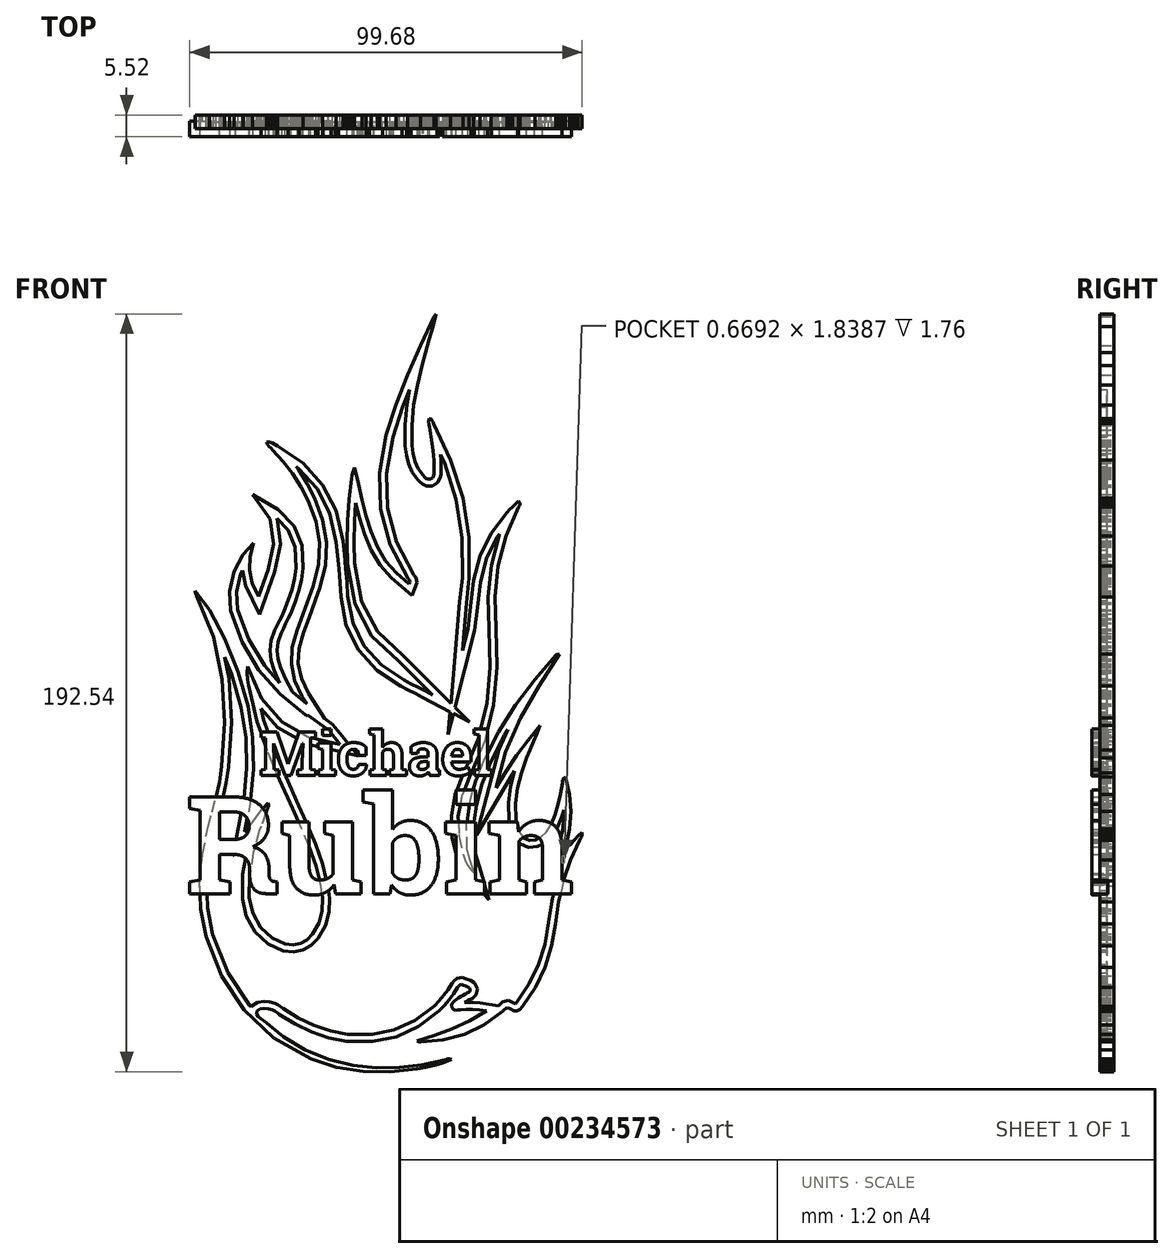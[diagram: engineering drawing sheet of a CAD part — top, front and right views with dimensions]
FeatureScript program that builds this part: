
annotation { "Feature Type Name" : "Feature", "Feature Type Description" : "" }
export const myFeature = defineFeature(function(context is Context, id is Id, definition is map)
    precondition{}
    {
        {
            var Q0;
            Q0=qCreatedBy(makeId("Front.planeOp"),FACE);
            var sketch = newSketch(context, id + "F0", { "sketchPlane" : qUnion([Q0])});
            skLineSegment(sketch, "E0", {"start": v(36.22, -211.62) * mm, "end": v(31.33, -213.63) * mm});
            skLineSegment(sketch, "E1", {"start": v(31.33, -213.63) * mm, "end": v(26.4, -215.17) * mm});
            skLineSegment(sketch, "E2", {"start": v(26.4, -215.17) * mm, "end": v(21.44, -216.32) * mm});
            skLineSegment(sketch, "E3", {"start": v(21.44, -216.32) * mm, "end": v(16.46, -217.18) * mm});
            skLineSegment(sketch, "E4", {"start": v(16.46, -217.18) * mm, "end": v(0.82, -218.8) * mm});
            skLineSegment(sketch, "E5", {"start": v(0.82, -218.8) * mm, "end": v(-14.67, -218.69) * mm});
            skLineSegment(sketch, "E6", {"start": v(-14.67, -218.69) * mm, "end": v(-29.95, -216.4) * mm});
            skLineSegment(sketch, "E7", {"start": v(-29.95, -216.4) * mm, "end": v(-44.93, -211.45) * mm});
            skLineSegment(sketch, "E8", {"start": v(-44.93, -211.45) * mm, "end": v(-66.37, -199.2) * mm});
            skLineSegment(sketch, "E9", {"start": v(-66.37, -199.2) * mm, "end": v(-83.45, -183.16) * mm});
            skLineSegment(sketch, "E10", {"start": v(-83.45, -183.16) * mm, "end": v(-96.43, -163.58) * mm});
            skLineSegment(sketch, "E11", {"start": v(-96.43, -163.58) * mm, "end": v(-105.51, -140.68) * mm});
            skLineSegment(sketch, "E12", {"start": v(-105.51, -140.68) * mm, "end": v(-108.67, -124.82) * mm});
            skLineSegment(sketch, "E13", {"start": v(-108.67, -124.82) * mm, "end": v(-109.13, -109.02) * mm});
            skLineSegment(sketch, "E14", {"start": v(-109.13, -109.02) * mm, "end": v(-107.45, -93.26) * mm});
            skLineSegment(sketch, "E15", {"start": v(-107.45, -93.26) * mm, "end": v(-104.2, -77.54) * mm});
            skLineSegment(sketch, "E16", {"start": v(-104.2, -77.54) * mm, "end": v(-101.94, -68.84) * mm});
            skLineSegment(sketch, "E17", {"start": v(-101.94, -68.84) * mm, "end": v(-99.7, -60.13) * mm});
            skLineSegment(sketch, "E18", {"start": v(-99.7, -60.13) * mm, "end": v(-97.73, -51.36) * mm});
            skLineSegment(sketch, "E19", {"start": v(-97.73, -51.36) * mm, "end": v(-96.35, -42.46) * mm});
            skLineSegment(sketch, "E20", {"start": v(-96.35, -42.46) * mm, "end": v(-94.74, -17.12) * mm});
            skLineSegment(sketch, "E21", {"start": v(-94.74, -17.12) * mm, "end": v(-96.1, 7.8) * mm});
            skLineSegment(sketch, "E22", {"start": v(-96.1, 7.8) * mm, "end": v(-101.2, 32.15) * mm});
            skLineSegment(sketch, "E23", {"start": v(-101.2, 32.15) * mm, "end": v(-110.82, 55.85) * mm});
            skLineSegment(sketch, "E24", {"start": v(-110.82, 55.85) * mm, "end": v(-111.04, 56.3) * mm});
            skLineSegment(sketch, "E25", {"start": v(-111.04, 56.3) * mm, "end": v(-111.25, 56.75) * mm});
            skLineSegment(sketch, "E26", {"start": v(-111.25, 56.75) * mm, "end": v(-111.45, 57.2) * mm});
            skLineSegment(sketch, "E27", {"start": v(-111.45, 57.2) * mm, "end": v(-111.63, 57.67) * mm});
            skLineSegment(sketch, "E28", {"start": v(-111.63, 57.67) * mm, "end": v(-111.68, 57.9) * mm});
            skLineSegment(sketch, "E29", {"start": v(-111.68, 57.9) * mm, "end": v(-111.7, 58.14) * mm});
            skLineSegment(sketch, "E30", {"start": v(-111.7, 58.14) * mm, "end": v(-111.7, 58.38) * mm});
            skLineSegment(sketch, "E31", {"start": v(-111.7, 58.38) * mm, "end": v(-111.71, 58.63) * mm});
            skLineSegment(sketch, "E32", {"start": v(-111.71, 58.63) * mm, "end": v(-103.48, 47.66) * mm});
            skLineSegment(sketch, "E33", {"start": v(-103.48, 47.66) * mm, "end": v(-94.75, 31.33) * mm});
            skLineSegment(sketch, "E34", {"start": v(-94.75, 31.33) * mm, "end": v(-86.88, 12.12) * mm});
            skLineSegment(sketch, "E35", {"start": v(-86.88, 12.12) * mm, "end": v(-81.23, -7.5) * mm});
            skLineSegment(sketch, "E36", {"start": v(-81.23, -7.5) * mm, "end": v(-78.47, -25.75) * mm});
            skLineSegment(sketch, "E37", {"start": v(-78.47, -25.75) * mm, "end": v(-77.98, -43.94) * mm});
            skLineSegment(sketch, "E38", {"start": v(-77.98, -43.94) * mm, "end": v(-79.6, -62.1) * mm});
            skLineSegment(sketch, "E39", {"start": v(-79.6, -62.1) * mm, "end": v(-83.23, -80.25) * mm});
            skLineSegment(sketch, "E40", {"start": v(-83.23, -80.25) * mm, "end": v(-79.71, -76.18) * mm});
            skLineSegment(sketch, "E41", {"start": v(-79.71, -76.18) * mm, "end": v(-76.5, -71.93) * mm});
            skLineSegment(sketch, "E42", {"start": v(-76.5, -71.93) * mm, "end": v(-73.28, -67.72) * mm});
            skLineSegment(sketch, "E43", {"start": v(-73.28, -67.72) * mm, "end": v(-69.75, -63.75) * mm});
            skLineSegment(sketch, "E44", {"start": v(-69.75, -63.75) * mm, "end": v(-69.26, -64.86) * mm});
            skLineSegment(sketch, "E45", {"start": v(-69.26, -64.86) * mm, "end": v(-69.38, -65.8) * mm});
            skLineSegment(sketch, "E46", {"start": v(-69.38, -65.8) * mm, "end": v(-69.82, -66.66) * mm});
            skLineSegment(sketch, "E47", {"start": v(-69.82, -66.66) * mm, "end": v(-70.24, -67.47) * mm});
            skLineSegment(sketch, "E48", {"start": v(-70.24, -67.47) * mm, "end": v(-74.68, -79.84) * mm});
            skLineSegment(sketch, "E49", {"start": v(-74.68, -79.84) * mm, "end": v(-78.17, -92.4) * mm});
            skLineSegment(sketch, "E50", {"start": v(-78.17, -92.4) * mm, "end": v(-80.25, -105.26) * mm});
            skLineSegment(sketch, "E51", {"start": v(-80.25, -105.26) * mm, "end": v(-80.49, -118.5) * mm});
            skLineSegment(sketch, "E52", {"start": v(-80.49, -118.5) * mm, "end": v(-78.44, -127.45) * mm});
            skLineSegment(sketch, "E53", {"start": v(-78.44, -127.45) * mm, "end": v(-73.87, -135.48) * mm});
            skLineSegment(sketch, "E54", {"start": v(-73.87, -135.48) * mm, "end": v(-67.44, -141.67) * mm});
            skLineSegment(sketch, "E55", {"start": v(-67.44, -141.67) * mm, "end": v(-59.81, -145.14) * mm});
            skLineSegment(sketch, "E56", {"start": v(-59.81, -145.14) * mm, "end": v(-55.14, -145.6) * mm});
            skLineSegment(sketch, "E57", {"start": v(-55.14, -145.6) * mm, "end": v(-50.93, -144.78) * mm});
            skLineSegment(sketch, "E58", {"start": v(-50.93, -144.78) * mm, "end": v(-47.2, -142.69) * mm});
            skLineSegment(sketch, "E59", {"start": v(-47.2, -142.69) * mm, "end": v(-43.94, -139.34) * mm});
            skLineSegment(sketch, "E60", {"start": v(-43.94, -139.34) * mm, "end": v(-40.24, -132.83) * mm});
            skLineSegment(sketch, "E61", {"start": v(-40.24, -132.83) * mm, "end": v(-38.48, -125.96) * mm});
            skLineSegment(sketch, "E62", {"start": v(-38.48, -125.96) * mm, "end": v(-38.25, -118.85) * mm});
            skLineSegment(sketch, "E63", {"start": v(-38.25, -118.85) * mm, "end": v(-39.12, -111.62) * mm});
            skLineSegment(sketch, "E64", {"start": v(-39.12, -111.62) * mm, "end": v(-41.97, -99.94) * mm});
            skLineSegment(sketch, "E65", {"start": v(-41.97, -99.94) * mm, "end": v(-45.97, -88.66) * mm});
            skLineSegment(sketch, "E66", {"start": v(-45.97, -88.66) * mm, "end": v(-50.67, -77.63) * mm});
            skLineSegment(sketch, "E67", {"start": v(-50.67, -77.63) * mm, "end": v(-55.6, -66.69) * mm});
            skLineSegment(sketch, "E68", {"start": v(-55.6, -66.69) * mm, "end": v(-62.97, -50.27) * mm});
            skLineSegment(sketch, "E69", {"start": v(-62.97, -50.27) * mm, "end": v(-69.97, -33.73) * mm});
            skLineSegment(sketch, "E70", {"start": v(-69.97, -33.73) * mm, "end": v(-75.91, -16.8) * mm});
            skLineSegment(sketch, "E71", {"start": v(-75.91, -16.8) * mm, "end": v(-80.13, 0.76) * mm});
            skLineSegment(sketch, "E72", {"start": v(-80.13, 0.76) * mm, "end": v(-80.78, 4.25) * mm});
            skLineSegment(sketch, "E73", {"start": v(-80.78, 4.25) * mm, "end": v(-81.36, 7.8) * mm});
            skLineSegment(sketch, "E74", {"start": v(-81.36, 7.8) * mm, "end": v(-81.65, 11.46) * mm});
            skLineSegment(sketch, "E75", {"start": v(-81.65, 11.46) * mm, "end": v(-81.44, 15.32) * mm});
            skLineSegment(sketch, "E76", {"start": v(-81.44, 15.32) * mm, "end": v(-73.38, -3.27) * mm});
            skLineSegment(sketch, "E77", {"start": v(-73.38, -3.27) * mm, "end": v(-61.5, -16.8) * mm});
            skLineSegment(sketch, "E78", {"start": v(-61.5, -16.8) * mm, "end": v(-46.23, -25.6) * mm});
            skLineSegment(sketch, "E79", {"start": v(-46.23, -25.6) * mm, "end": v(-28, -29.97) * mm});
            skLineSegment(sketch, "E80", {"start": v(-28, -29.97) * mm, "end": v(-30.14, -27.34) * mm});
            skLineSegment(sketch, "E81", {"start": v(-30.14, -27.34) * mm, "end": v(-32.52, -24.4) * mm});
            skLineSegment(sketch, "E82", {"start": v(-32.52, -24.4) * mm, "end": v(-35.1, -21.27) * mm});
            skLineSegment(sketch, "E83", {"start": v(-47.22, -6.45) * mm, "end": v(-49.9, -2.22) * mm});
            skLineSegment(sketch, "E84", {"start": v(-49.9, -2.22) * mm, "end": v(-54.2, 7.07) * mm});
            skLineSegment(sketch, "E85", {"start": v(-54.2, 7.07) * mm, "end": v(-56.2, 16.53) * mm});
            skLineSegment(sketch, "E86", {"start": v(-56.2, 16.53) * mm, "end": v(-55.8, 26.19) * mm});
            skLineSegment(sketch, "E87", {"start": v(-55.8, 26.19) * mm, "end": v(-52.98, 36.09) * mm});
            skLineSegment(sketch, "E88", {"start": v(-52.98, 36.09) * mm, "end": v(-50.54, 42.37) * mm});
            skLineSegment(sketch, "E89", {"start": v(-50.54, 42.37) * mm, "end": v(-48.24, 48.72) * mm});
            skLineSegment(sketch, "E90", {"start": v(-48.24, 48.72) * mm, "end": v(-45.98, 55.08) * mm});
            skLineSegment(sketch, "E91", {"start": v(-45.98, 55.08) * mm, "end": v(-43.67, 61.42) * mm});
            skLineSegment(sketch, "E92", {"start": v(-43.67, 61.42) * mm, "end": v(-40.4, 74.02) * mm});
            skLineSegment(sketch, "E93", {"start": v(-40.4, 74.02) * mm, "end": v(-39.92, 86.47) * mm});
            skLineSegment(sketch, "E94", {"start": v(-39.92, 86.47) * mm, "end": v(-42, 98.76) * mm});
            skLineSegment(sketch, "E95", {"start": v(-42, 98.76) * mm, "end": v(-46.45, 110.92) * mm});
            skLineSegment(sketch, "E96", {"start": v(-46.45, 110.92) * mm, "end": v(-50.6, 118.94) * mm});
            skLineSegment(sketch, "E97", {"start": v(-50.6, 118.94) * mm, "end": v(-55.4, 126.5) * mm});
            skLineSegment(sketch, "E98", {"start": v(-55.4, 126.5) * mm, "end": v(-60.87, 133.6) * mm});
            skLineSegment(sketch, "E99", {"start": v(-60.87, 133.6) * mm, "end": v(-66.94, 140.29) * mm});
            skLineSegment(sketch, "E100", {"start": v(-66.94, 140.29) * mm, "end": v(-67.94, 141.2) * mm});
            skLineSegment(sketch, "E101", {"start": v(-67.94, 141.2) * mm, "end": v(-68.96, 142.15) * mm});
            skLineSegment(sketch, "E102", {"start": v(-68.96, 142.15) * mm, "end": v(-69.86, 143.3) * mm});
            skLineSegment(sketch, "E103", {"start": v(-69.86, 143.3) * mm, "end": v(-70.49, 144.84) * mm});
            skLineSegment(sketch, "E104", {"start": v(-70.49, 144.84) * mm, "end": v(-68.66, 144.75) * mm});
            skLineSegment(sketch, "E105", {"start": v(-68.66, 144.75) * mm, "end": v(-67.03, 144.2) * mm});
            skLineSegment(sketch, "E106", {"start": v(-67.03, 144.2) * mm, "end": v(-65.55, 143.41) * mm});
            skLineSegment(sketch, "E107", {"start": v(-65.55, 143.41) * mm, "end": v(-64.11, 142.6) * mm});
            skLineSegment(sketch, "E108", {"start": v(-64.11, 142.6) * mm, "end": v(-49.3, 132.58) * mm});
            skLineSegment(sketch, "E109", {"start": v(-49.3, 132.58) * mm, "end": v(-38.08, 120.08) * mm});
            skLineSegment(sketch, "E110", {"start": v(-38.08, 120.08) * mm, "end": v(-30.44, 105.13) * mm});
            skLineSegment(sketch, "E111", {"start": v(-30.44, 105.13) * mm, "end": v(-26.4, 87.74) * mm});
            skLineSegment(sketch, "E112", {"start": v(-26.4, 87.74) * mm, "end": v(-25.52, 79.8) * mm});
            skLineSegment(sketch, "E113", {"start": v(-25.52, 79.8) * mm, "end": v(-24.78, 71.84) * mm});
            skLineSegment(sketch, "E114", {"start": v(-24.78, 71.84) * mm, "end": v(-24.15, 63.88) * mm});
            skLineSegment(sketch, "E115", {"start": v(-24.15, 63.88) * mm, "end": v(-23.61, 55.9) * mm});
            skLineSegment(sketch, "E116", {"start": v(-23.61, 55.9) * mm, "end": v(-20.68, 40.23) * mm});
            skLineSegment(sketch, "E117", {"start": v(-20.68, 40.23) * mm, "end": v(-14.12, 27) * mm});
            skLineSegment(sketch, "E118", {"start": v(-14.12, 27) * mm, "end": v(-4.17, 16.07) * mm});
            skLineSegment(sketch, "E119", {"start": v(-4.17, 16.07) * mm, "end": v(8.95, 7.26) * mm});
            skLineSegment(sketch, "E120", {"start": v(8.95, 7.26) * mm, "end": v(13.05, 5.13) * mm});
            skLineSegment(sketch, "E121", {"start": v(13.05, 5.13) * mm, "end": v(17.18, 3.04) * mm});
            skLineSegment(sketch, "E122", {"start": v(17.18, 3.04) * mm, "end": v(21.3, 0.95) * mm});
            skLineSegment(sketch, "E123", {"start": v(21.3, 0.95) * mm, "end": v(25.39, -1.2) * mm});
            skLineSegment(sketch, "E124", {"start": v(42.57, 24.32) * mm, "end": v(45.76, 36.8) * mm});
            skLineSegment(sketch, "E125", {"start": v(45.76, 36.8) * mm, "end": v(47.38, 49.8) * mm});
            skLineSegment(sketch, "E126", {"start": v(47.38, 49.8) * mm, "end": v(49.12, 64.7) * mm});
            skLineSegment(sketch, "E127", {"start": v(49.12, 64.7) * mm, "end": v(52.83, 78.86) * mm});
            skLineSegment(sketch, "E128", {"start": v(52.83, 78.86) * mm, "end": v(59.04, 92.06) * mm});
            skLineSegment(sketch, "E129", {"start": v(59.04, 92.06) * mm, "end": v(68.25, 104.1) * mm});
            skLineSegment(sketch, "E130", {"start": v(68.25, 104.1) * mm, "end": v(69.9, 105.76) * mm});
            skLineSegment(sketch, "E131", {"start": v(69.9, 105.76) * mm, "end": v(71.6, 107.38) * mm});
            skLineSegment(sketch, "E132", {"start": v(71.6, 107.38) * mm, "end": v(73.33, 108.98) * mm});
            skLineSegment(sketch, "E133", {"start": v(73.33, 108.98) * mm, "end": v(75.04, 110.6) * mm});
            skLineSegment(sketch, "E134", {"start": v(75.04, 110.6) * mm, "end": v(75.8, 109.58) * mm});
            skLineSegment(sketch, "E135", {"start": v(75.8, 109.58) * mm, "end": v(75.83, 108.72) * mm});
            skLineSegment(sketch, "E136", {"start": v(75.83, 108.72) * mm, "end": v(75.46, 107.99) * mm});
            skLineSegment(sketch, "E137", {"start": v(75.46, 107.99) * mm, "end": v(75.03, 107.33) * mm});
            skLineSegment(sketch, "E138", {"start": v(75.03, 107.33) * mm, "end": v(67.67, 90.5) * mm});
            skLineSegment(sketch, "E139", {"start": v(67.67, 90.5) * mm, "end": v(63.25, 73.12) * mm});
            skLineSegment(sketch, "E140", {"start": v(63.25, 73.12) * mm, "end": v(61.45, 55.28) * mm});
            skLineSegment(sketch, "E141", {"start": v(61.45, 55.28) * mm, "end": v(61.96, 37.07) * mm});
            skLineSegment(sketch, "E142", {"start": v(61.96, 37.07) * mm, "end": v(62.65, 14.79) * mm});
            skLineSegment(sketch, "E143", {"start": v(62.65, 14.79) * mm, "end": v(60.62, -6.94) * mm});
            skLineSegment(sketch, "E144", {"start": v(60.62, -6.94) * mm, "end": v(55.44, -28.12) * mm});
            skLineSegment(sketch, "E145", {"start": v(55.44, -28.12) * mm, "end": v(46.7, -48.74) * mm});
            skLineSegment(sketch, "E146", {"start": v(46.7, -48.74) * mm, "end": v(42.2, -59.87) * mm});
            skLineSegment(sketch, "E147", {"start": v(42.2, -59.87) * mm, "end": v(40.19, -71.32) * mm});
            skLineSegment(sketch, "E148", {"start": v(40.19, -71.32) * mm, "end": v(40.61, -83) * mm});
            skLineSegment(sketch, "E149", {"start": v(40.61, -83) * mm, "end": v(43.43, -94.83) * mm});
            skLineSegment(sketch, "E150", {"start": v(43.43, -94.83) * mm, "end": v(44.5, -97.48) * mm});
            skLineSegment(sketch, "E151", {"start": v(44.5, -97.48) * mm, "end": v(45.83, -99.98) * mm});
            skLineSegment(sketch, "E152", {"start": v(45.83, -99.98) * mm, "end": v(47.47, -102.3) * mm});
            skLineSegment(sketch, "E153", {"start": v(47.47, -102.3) * mm, "end": v(49.44, -104.44) * mm});
            skLineSegment(sketch, "E154", {"start": v(49.44, -104.44) * mm, "end": v(48.39, -100.83) * mm});
            skLineSegment(sketch, "E155", {"start": v(48.39, -100.83) * mm, "end": v(47.2, -97.27) * mm});
            skLineSegment(sketch, "E156", {"start": v(47.2, -97.27) * mm, "end": v(46.1, -93.68) * mm});
            skLineSegment(sketch, "E157", {"start": v(46.1, -93.68) * mm, "end": v(45.39, -89.98) * mm});
            skLineSegment(sketch, "E158", {"start": v(45.39, -89.98) * mm, "end": v(45, -76.7) * mm});
            skLineSegment(sketch, "E159", {"start": v(45, -76.7) * mm, "end": v(46.72, -63.83) * mm});
            skLineSegment(sketch, "E160", {"start": v(46.72, -63.83) * mm, "end": v(50.17, -51.3) * mm});
            skLineSegment(sketch, "E161", {"start": v(50.17, -51.3) * mm, "end": v(54.97, -39.06) * mm});
            skLineSegment(sketch, "E162", {"start": v(54.97, -39.06) * mm, "end": v(63.36, -22.5) * mm});
            skLineSegment(sketch, "E163", {"start": v(63.36, -22.5) * mm, "end": v(73.26, -6.97) * mm});
            skLineSegment(sketch, "E164", {"start": v(73.26, -6.97) * mm, "end": v(84.41, 7.72) * mm});
            skLineSegment(sketch, "E165", {"start": v(84.41, 7.72) * mm, "end": v(96.56, 21.71) * mm});
            skLineSegment(sketch, "E166", {"start": v(96.56, 21.71) * mm, "end": v(96.76, 21.85) * mm});
            skLineSegment(sketch, "E167", {"start": v(96.76, 21.85) * mm, "end": v(97.11, 21.99) * mm});
            skLineSegment(sketch, "E168", {"start": v(97.11, 21.99) * mm, "end": v(97.69, 22.19) * mm});
            skLineSegment(sketch, "E169", {"start": v(97.69, 22.19) * mm, "end": v(98.57, 22.52) * mm});
            skLineSegment(sketch, "E170", {"start": v(98.57, 22.52) * mm, "end": v(86.8, 4.05) * mm});
            skLineSegment(sketch, "E171", {"start": v(86.8, 4.05) * mm, "end": v(76.17, -14.66) * mm});
            skLineSegment(sketch, "E172", {"start": v(76.17, -14.66) * mm, "end": v(67.6, -34.16) * mm});
            skLineSegment(sketch, "E173", {"start": v(67.6, -34.16) * mm, "end": v(62.07, -54.97) * mm});
            skLineSegment(sketch, "E174", {"start": v(62.07, -54.97) * mm, "end": v(67.68, -45.45) * mm});
            skLineSegment(sketch, "E175", {"start": v(67.68, -45.45) * mm, "end": v(73.74, -36.24) * mm});
            skLineSegment(sketch, "E176", {"start": v(73.74, -36.24) * mm, "end": v(80.33, -27.4) * mm});
            skLineSegment(sketch, "E177", {"start": v(80.33, -27.4) * mm, "end": v(87.52, -18.94) * mm});
            skLineSegment(sketch, "E178", {"start": v(87.52, -18.94) * mm, "end": v(85.53, -23.6) * mm});
            skLineSegment(sketch, "E179", {"start": v(85.53, -23.6) * mm, "end": v(83.53, -28.25) * mm});
            skLineSegment(sketch, "E180", {"start": v(83.53, -28.25) * mm, "end": v(81.56, -32.91) * mm});
            skLineSegment(sketch, "E181", {"start": v(81.56, -32.91) * mm, "end": v(79.66, -37.6) * mm});
            skLineSegment(sketch, "E182", {"start": v(79.66, -37.6) * mm, "end": v(76.58, -46.2) * mm});
            skLineSegment(sketch, "E183", {"start": v(76.58, -46.2) * mm, "end": v(74.32, -54.96) * mm});
            skLineSegment(sketch, "E184", {"start": v(74.32, -54.96) * mm, "end": v(73.2, -63.92) * mm});
            skLineSegment(sketch, "E185", {"start": v(73.2, -63.92) * mm, "end": v(73.53, -73.14) * mm});
            skLineSegment(sketch, "E186", {"start": v(73.53, -73.14) * mm, "end": v(74.54, -77.85) * mm});
            skLineSegment(sketch, "E187", {"start": v(74.54, -77.85) * mm, "end": v(76.22, -81.55) * mm});
            skLineSegment(sketch, "E188", {"start": v(76.22, -81.55) * mm, "end": v(78.53, -84.06) * mm});
            skLineSegment(sketch, "E189", {"start": v(78.53, -84.06) * mm, "end": v(81.4, -85.22) * mm});
            skLineSegment(sketch, "E190", {"start": v(81.4, -85.22) * mm, "end": v(84.75, -84.93) * mm});
            skLineSegment(sketch, "E191", {"start": v(84.75, -84.93) * mm, "end": v(88.08, -83.26) * mm});
            skLineSegment(sketch, "E192", {"start": v(88.08, -83.26) * mm, "end": v(91.12, -80.4) * mm});
            skLineSegment(sketch, "E193", {"start": v(91.12, -80.4) * mm, "end": v(93.6, -76.56) * mm});
            skLineSegment(sketch, "E194", {"start": v(93.6, -76.56) * mm, "end": v(96.06, -70.66) * mm});
            skLineSegment(sketch, "E195", {"start": v(96.06, -70.66) * mm, "end": v(97.89, -64.58) * mm});
            skLineSegment(sketch, "E196", {"start": v(97.89, -64.58) * mm, "end": v(99.25, -58.37) * mm});
            skLineSegment(sketch, "E197", {"start": v(99.25, -58.37) * mm, "end": v(100.34, -52.08) * mm});
            skLineSegment(sketch, "E198", {"start": v(100.34, -52.08) * mm, "end": v(100.4, -51.25) * mm});
            skLineSegment(sketch, "E199", {"start": v(100.4, -51.25) * mm, "end": v(100.5, -50.37) * mm});
            skLineSegment(sketch, "E200", {"start": v(100.5, -50.37) * mm, "end": v(100.95, -49.5) * mm});
            skLineSegment(sketch, "E201", {"start": v(100.95, -49.5) * mm, "end": v(102, -48.7) * mm});
            skLineSegment(sketch, "E202", {"start": v(102, -48.7) * mm, "end": v(104.38, -58.6) * mm});
            skLineSegment(sketch, "E203", {"start": v(104.38, -58.6) * mm, "end": v(105.2, -68.56) * mm});
            skLineSegment(sketch, "E204", {"start": v(105.2, -68.56) * mm, "end": v(104.5, -78.65) * mm});
            skLineSegment(sketch, "E205", {"start": v(104.5, -78.65) * mm, "end": v(102.35, -88.96) * mm});
            skLineSegment(sketch, "E206", {"start": v(102.35, -88.96) * mm, "end": v(105.22, -87.14) * mm});
            skLineSegment(sketch, "E207", {"start": v(105.22, -87.14) * mm, "end": v(107.32, -84.86) * mm});
            skLineSegment(sketch, "E208", {"start": v(107.32, -84.86) * mm, "end": v(109.25, -82.56) * mm});
            skLineSegment(sketch, "E209", {"start": v(109.25, -82.56) * mm, "end": v(111.61, -80.72) * mm});
            skLineSegment(sketch, "E210", {"start": v(111.61, -80.72) * mm, "end": v(111.71, -82.05) * mm});
            skLineSegment(sketch, "E211", {"start": v(111.71, -82.05) * mm, "end": v(111.37, -83.19) * mm});
            skLineSegment(sketch, "E212", {"start": v(111.37, -83.19) * mm, "end": v(110.8, -84.2) * mm});
            skLineSegment(sketch, "E213", {"start": v(110.8, -84.2) * mm, "end": v(110.22, -85.16) * mm});
            skLineSegment(sketch, "E214", {"start": v(110.22, -85.16) * mm, "end": v(104.88, -96.66) * mm});
            skLineSegment(sketch, "E215", {"start": v(104.88, -96.66) * mm, "end": v(100.95, -108.55) * mm});
            skLineSegment(sketch, "E216", {"start": v(100.95, -108.55) * mm, "end": v(98.19, -120.79) * mm});
            skLineSegment(sketch, "E217", {"start": v(98.19, -120.79) * mm, "end": v(96.34, -133.33) * mm});
            skLineSegment(sketch, "E218", {"start": v(96.34, -133.33) * mm, "end": v(94.07, -146.18) * mm});
            skLineSegment(sketch, "E219", {"start": v(94.07, -146.18) * mm, "end": v(90.2, -158.45) * mm});
            skLineSegment(sketch, "E220", {"start": v(90.2, -158.45) * mm, "end": v(84.66, -170.07) * mm});
            skLineSegment(sketch, "E221", {"start": v(84.66, -170.07) * mm, "end": v(77.33, -180.99) * mm});
            skLineSegment(sketch, "E222", {"start": v(77.33, -180.99) * mm, "end": v(75.79, -182.68) * mm});
            skLineSegment(sketch, "E223", {"start": v(75.79, -182.68) * mm, "end": v(74.16, -183.69) * mm});
            skLineSegment(sketch, "E224", {"start": v(74.16, -183.69) * mm, "end": v(72.35, -183.76) * mm});
            skLineSegment(sketch, "E225", {"start": v(72.35, -183.76) * mm, "end": v(70.27, -182.65) * mm});
            skLineSegment(sketch, "E226", {"start": v(70.27, -182.65) * mm, "end": v(68.78, -181.95) * mm});
            skLineSegment(sketch, "E227", {"start": v(68.78, -181.95) * mm, "end": v(67.62, -182.25) * mm});
            skLineSegment(sketch, "E228", {"start": v(67.62, -182.25) * mm, "end": v(66.67, -183.1) * mm});
            skLineSegment(sketch, "E229", {"start": v(66.67, -183.1) * mm, "end": v(65.76, -184.05) * mm});
            skLineSegment(sketch, "E230", {"start": v(65.76, -184.05) * mm, "end": v(55.2, -191.78) * mm});
            skLineSegment(sketch, "E231", {"start": v(55.2, -191.78) * mm, "end": v(43.77, -197.16) * mm});
            skLineSegment(sketch, "E232", {"start": v(43.77, -197.16) * mm, "end": v(31.53, -200.4) * mm});
            skLineSegment(sketch, "E233", {"start": v(31.53, -200.4) * mm, "end": v(18.58, -201.72) * mm});
            skLineSegment(sketch, "E234", {"start": v(18.58, -201.72) * mm, "end": v(18.1, -201.7) * mm});
            skLineSegment(sketch, "E235", {"start": v(18.1, -201.7) * mm, "end": v(17.6, -201.61) * mm});
            skLineSegment(sketch, "E236", {"start": v(17.6, -201.61) * mm, "end": v(17.06, -201.42) * mm});
            skLineSegment(sketch, "E237", {"start": v(17.06, -201.42) * mm, "end": v(16.5, -201.12) * mm});
            skLineSegment(sketch, "E238", {"start": v(16.5, -201.12) * mm, "end": v(26.6, -197.86) * mm});
            skLineSegment(sketch, "E239", {"start": v(26.6, -197.86) * mm, "end": v(36.68, -194.15) * mm});
            skLineSegment(sketch, "E240", {"start": v(36.68, -194.15) * mm, "end": v(46.66, -189.57) * mm});
            skLineSegment(sketch, "E241", {"start": v(46.66, -189.57) * mm, "end": v(56.54, -183.68) * mm});
            skLineSegment(sketch, "E242", {"start": v(56.54, -183.68) * mm, "end": v(52.32, -183.03) * mm});
            skLineSegment(sketch, "E243", {"start": v(52.32, -183.03) * mm, "end": v(48.47, -182.8) * mm});
            skLineSegment(sketch, "E244", {"start": v(48.47, -182.8) * mm, "end": v(44.87, -182.84) * mm});
            skLineSegment(sketch, "E245", {"start": v(44.87, -182.84) * mm, "end": v(41.39, -183.05) * mm});
            skLineSegment(sketch, "E246", {"start": v(41.39, -183.05) * mm, "end": v(39.98, -183.22) * mm});
            skLineSegment(sketch, "E247", {"start": v(39.98, -183.22) * mm, "end": v(38.59, -183.3) * mm});
            skLineSegment(sketch, "E248", {"start": v(38.59, -183.3) * mm, "end": v(37.38, -182.97) * mm});
            skLineSegment(sketch, "E249", {"start": v(37.38, -182.97) * mm, "end": v(36.5, -181.87) * mm});
            skLineSegment(sketch, "E250", {"start": v(36.5, -181.87) * mm, "end": v(36.3, -180.34) * mm});
            skLineSegment(sketch, "E251", {"start": v(36.3, -180.34) * mm, "end": v(36.88, -179.06) * mm});
            skLineSegment(sketch, "E252", {"start": v(36.88, -179.06) * mm, "end": v(37.93, -177.98) * mm});
            skLineSegment(sketch, "E253", {"start": v(37.93, -177.98) * mm, "end": v(39.17, -177.05) * mm});
            skLineSegment(sketch, "E254", {"start": v(39.17, -177.05) * mm, "end": v(40.42, -176.23) * mm});
            skLineSegment(sketch, "E255", {"start": v(40.42, -176.23) * mm, "end": v(41.7, -175.46) * mm});
            skLineSegment(sketch, "E256", {"start": v(41.7, -175.46) * mm, "end": v(43, -174.7) * mm});
            skLineSegment(sketch, "E257", {"start": v(43, -174.7) * mm, "end": v(44.27, -173.9) * mm});
            skLineSegment(sketch, "E258", {"start": v(44.27, -173.9) * mm, "end": v(45.19, -173.43) * mm});
            skLineSegment(sketch, "E259", {"start": v(45.19, -173.43) * mm, "end": v(46.16, -172.98) * mm});
            skLineSegment(sketch, "E260", {"start": v(46.16, -172.98) * mm, "end": v(46.89, -172.38) * mm});
            skLineSegment(sketch, "E261", {"start": v(46.89, -172.38) * mm, "end": v(47.1, -171.45) * mm});
            skLineSegment(sketch, "E262", {"start": v(47.1, -171.45) * mm, "end": v(46.56, -170.35) * mm});
            skLineSegment(sketch, "E263", {"start": v(46.56, -170.35) * mm, "end": v(45.53, -169.75) * mm});
            skLineSegment(sketch, "E264", {"start": v(45.53, -169.75) * mm, "end": v(44.3, -169.36) * mm});
            skLineSegment(sketch, "E265", {"start": v(44.3, -169.36) * mm, "end": v(43.15, -168.89) * mm});
            skLineSegment(sketch, "E266", {"start": v(43.15, -168.89) * mm, "end": v(42.12, -168.52) * mm});
            skLineSegment(sketch, "E267", {"start": v(42.12, -168.52) * mm, "end": v(41.25, -168.68) * mm});
            skLineSegment(sketch, "E268", {"start": v(41.25, -168.68) * mm, "end": v(40.5, -169.24) * mm});
            skLineSegment(sketch, "E269", {"start": v(40.5, -169.24) * mm, "end": v(39.88, -170.1) * mm});
            skLineSegment(sketch, "E270", {"start": v(39.88, -170.1) * mm, "end": v(37.54, -173.8) * mm});
            skLineSegment(sketch, "E271", {"start": v(37.54, -173.8) * mm, "end": v(34.96, -177.32) * mm});
            skLineSegment(sketch, "E272", {"start": v(34.96, -177.32) * mm, "end": v(32.14, -180.65) * mm});
            skLineSegment(sketch, "E273", {"start": v(32.14, -180.65) * mm, "end": v(29.05, -183.76) * mm});
            skLineSegment(sketch, "E274", {"start": v(29.05, -183.76) * mm, "end": v(17.26, -192.74) * mm});
            skLineSegment(sketch, "E275", {"start": v(17.26, -192.74) * mm, "end": v(4.47, -198.6) * mm});
            skLineSegment(sketch, "E276", {"start": v(4.47, -198.6) * mm, "end": v(-9.33, -201.39) * mm});
            skLineSegment(sketch, "E277", {"start": v(-9.33, -201.39) * mm, "end": v(-24.16, -201.16) * mm});
            skLineSegment(sketch, "E278", {"start": v(-24.16, -201.16) * mm, "end": v(-34.7, -199.16) * mm});
            skLineSegment(sketch, "E279", {"start": v(-34.7, -199.16) * mm, "end": v(-44.65, -195.77) * mm});
            skLineSegment(sketch, "E280", {"start": v(-44.65, -195.77) * mm, "end": v(-54.11, -191.2) * mm});
            skLineSegment(sketch, "E281", {"start": v(-54.11, -191.2) * mm, "end": v(-63.2, -185.63) * mm});
            skLineSegment(sketch, "E282", {"start": v(-63.2, -185.63) * mm, "end": v(-64.11, -184.96) * mm});
            skLineSegment(sketch, "E283", {"start": v(-64.11, -184.96) * mm, "end": v(-65.02, -184.26) * mm});
            skLineSegment(sketch, "E284", {"start": v(-65.02, -184.26) * mm, "end": v(-65.94, -183.62) * mm});
            skLineSegment(sketch, "E285", {"start": v(-65.94, -183.62) * mm, "end": v(-66.93, -183.15) * mm});
            skLineSegment(sketch, "E286", {"start": v(-66.93, -183.15) * mm, "end": v(-69.38, -182.47) * mm});
            skLineSegment(sketch, "E287", {"start": v(-69.38, -182.47) * mm, "end": v(-71.92, -182.2) * mm});
            skLineSegment(sketch, "E288", {"start": v(-71.92, -182.2) * mm, "end": v(-74.2, -182.52) * mm});
            skLineSegment(sketch, "E289", {"start": v(-74.2, -182.52) * mm, "end": v(-75.86, -183.62) * mm});
            skLineSegment(sketch, "E290", {"start": v(-75.86, -183.62) * mm, "end": v(-76.28, -185.29) * mm});
            skLineSegment(sketch, "E291", {"start": v(-76.28, -185.29) * mm, "end": v(-75.27, -186.8) * mm});
            skLineSegment(sketch, "E292", {"start": v(-75.27, -186.8) * mm, "end": v(-73.58, -188.18) * mm});
            skLineSegment(sketch, "E293", {"start": v(-73.58, -188.18) * mm, "end": v(-71.96, -189.46) * mm});
            skLineSegment(sketch, "E294", {"start": v(-71.96, -189.46) * mm, "end": v(-60.55, -198.81) * mm});
            skLineSegment(sketch, "E295", {"start": v(-60.55, -198.81) * mm, "end": v(-48.19, -206.3) * mm});
            skLineSegment(sketch, "E296", {"start": v(-48.19, -206.3) * mm, "end": v(-34.84, -211.8) * mm});
            skLineSegment(sketch, "E297", {"start": v(-34.84, -211.8) * mm, "end": v(-20.44, -215.14) * mm});
            skLineSegment(sketch, "E298", {"start": v(-20.44, -215.14) * mm, "end": v(-7.1, -216.46) * mm});
            skLineSegment(sketch, "E299", {"start": v(-7.1, -216.46) * mm, "end": v(6.19, -216.4) * mm});
            skLineSegment(sketch, "E300", {"start": v(6.19, -216.4) * mm, "end": v(19.38, -214.9) * mm});
            skLineSegment(sketch, "E301", {"start": v(19.38, -214.9) * mm, "end": v(32.49, -211.9) * mm});
            skLineSegment(sketch, "E302", {"start": v(32.49, -211.9) * mm, "end": v(33.28, -211.61) * mm});
            skLineSegment(sketch, "E303", {"start": v(33.28, -211.61) * mm, "end": v(34.13, -211.33) * mm});
            skLineSegment(sketch, "E304", {"start": v(34.13, -211.33) * mm, "end": v(35.09, -211.26) * mm});
            skLineSegment(sketch, "E305", {"start": v(35.09, -211.26) * mm, "end": v(36.22, -211.62) * mm});
            skLineSegment(sketch, "E306", {"start": v(27.4, 218.8) * mm, "end": v(25.5, 211.32) * mm});
            skLineSegment(sketch, "E307", {"start": v(25.5, 211.32) * mm, "end": v(23.4, 203.9) * mm});
            skLineSegment(sketch, "E308", {"start": v(23.4, 203.9) * mm, "end": v(21.27, 196.49) * mm});
            skLineSegment(sketch, "E309", {"start": v(21.27, 196.49) * mm, "end": v(19.23, 189.05) * mm});
            skLineSegment(sketch, "E310", {"start": v(19.23, 189.05) * mm, "end": v(16.53, 177.6) * mm});
            skLineSegment(sketch, "E311", {"start": v(16.53, 177.6) * mm, "end": v(14.51, 166.07) * mm});
            skLineSegment(sketch, "E312", {"start": v(14.51, 166.07) * mm, "end": v(13.45, 154.43) * mm});
            skLineSegment(sketch, "E313", {"start": v(13.45, 154.43) * mm, "end": v(13.6, 142.64) * mm});
            skLineSegment(sketch, "E314", {"start": v(13.6, 142.64) * mm, "end": v(14.15, 138.02) * mm});
            skLineSegment(sketch, "E315", {"start": v(14.15, 138.02) * mm, "end": v(15.25, 133.59) * mm});
            skLineSegment(sketch, "E316", {"start": v(15.25, 133.59) * mm, "end": v(17.1, 129.43) * mm});
            skLineSegment(sketch, "E317", {"start": v(17.1, 129.43) * mm, "end": v(19.86, 125.63) * mm});
            skLineSegment(sketch, "E318", {"start": v(19.86, 125.63) * mm, "end": v(20.72, 124.68) * mm});
            skLineSegment(sketch, "E319", {"start": v(20.72, 124.68) * mm, "end": v(21.67, 123.83) * mm});
            skLineSegment(sketch, "E320", {"start": v(21.67, 123.83) * mm, "end": v(22.75, 123.32) * mm});
            skLineSegment(sketch, "E321", {"start": v(22.75, 123.32) * mm, "end": v(24.02, 123.38) * mm});
            skLineSegment(sketch, "E322", {"start": v(24.02, 123.38) * mm, "end": v(25.23, 124.13) * mm});
            skLineSegment(sketch, "E323", {"start": v(25.23, 124.13) * mm, "end": v(25.87, 125.27) * mm});
            skLineSegment(sketch, "E324", {"start": v(25.87, 125.27) * mm, "end": v(26.13, 126.62) * mm});
            skLineSegment(sketch, "E325", {"start": v(26.13, 126.62) * mm, "end": v(26.23, 128.02) * mm});
            skLineSegment(sketch, "E326", {"start": v(26.23, 128.02) * mm, "end": v(26.2, 134.02) * mm});
            skLineSegment(sketch, "E327", {"start": v(26.2, 134.02) * mm, "end": v(25.64, 139.98) * mm});
            skLineSegment(sketch, "E328", {"start": v(25.64, 139.98) * mm, "end": v(24.79, 145.9) * mm});
            skLineSegment(sketch, "E329", {"start": v(24.79, 145.9) * mm, "end": v(23.85, 151.83) * mm});
            skLineSegment(sketch, "E330", {"start": v(23.85, 151.83) * mm, "end": v(23.56, 153.4) * mm});
            skLineSegment(sketch, "E331", {"start": v(23.56, 153.4) * mm, "end": v(23.26, 154.98) * mm});
            skLineSegment(sketch, "E332", {"start": v(23.26, 154.98) * mm, "end": v(23.13, 156.59) * mm});
            skLineSegment(sketch, "E333", {"start": v(23.13, 156.59) * mm, "end": v(23.31, 158.23) * mm});
            skLineSegment(sketch, "E334", {"start": v(23.31, 158.23) * mm, "end": v(24.43, 157.94) * mm});
            skLineSegment(sketch, "E335", {"start": v(24.43, 157.94) * mm, "end": v(25.1, 157.26) * mm});
            skLineSegment(sketch, "E336", {"start": v(25.1, 157.26) * mm, "end": v(25.52, 156.4) * mm});
            skLineSegment(sketch, "E337", {"start": v(25.52, 156.4) * mm, "end": v(25.9, 155.53) * mm});
            skLineSegment(sketch, "E338", {"start": v(25.9, 155.53) * mm, "end": v(35.85, 134.31) * mm});
            skLineSegment(sketch, "E339", {"start": v(35.85, 134.31) * mm, "end": v(42.8, 112.4) * mm});
            skLineSegment(sketch, "E340", {"start": v(42.8, 112.4) * mm, "end": v(46.47, 89.72) * mm});
            skLineSegment(sketch, "E341", {"start": v(46.47, 89.72) * mm, "end": v(46.53, 66.23) * mm});
            skLineSegment(sketch, "E342", {"start": v(46.53, 66.23) * mm, "end": v(44.97, 51.93) * mm});
            skLineSegment(sketch, "E343", {"start": v(44.97, 51.93) * mm, "end": v(42.57, 24.32) * mm});
            skLineSegment(sketch, "E344", {"start": v(25.39, -1.2) * mm, "end": v(5.75, 18.49) * mm});
            skLineSegment(sketch, "E345", {"start": v(5.75, 18.49) * mm, "end": v(-9.73, 32.88) * mm});
            skLineSegment(sketch, "E346", {"start": v(-9.73, 32.88) * mm, "end": v(-19.47, 51.28) * mm});
            skLineSegment(sketch, "E347", {"start": v(-19.47, 51.28) * mm, "end": v(-23.68, 74.46) * mm});
            skLineSegment(sketch, "E348", {"start": v(-23.68, 74.46) * mm, "end": v(-24.05, 86.81) * mm});
            skLineSegment(sketch, "E349", {"start": v(-24.05, 86.81) * mm, "end": v(-23.76, 99.15) * mm});
            skLineSegment(sketch, "E350", {"start": v(-23.76, 99.15) * mm, "end": v(-22.89, 111.47) * mm});
            skLineSegment(sketch, "E351", {"start": v(-22.89, 111.47) * mm, "end": v(-21.51, 123.76) * mm});
            skLineSegment(sketch, "E352", {"start": v(-21.51, 123.76) * mm, "end": v(-21.26, 125.3) * mm});
            skLineSegment(sketch, "E353", {"start": v(-21.26, 125.3) * mm, "end": v(-20.88, 126.85) * mm});
            skLineSegment(sketch, "E354", {"start": v(-20.88, 126.85) * mm, "end": v(-20.35, 128.4) * mm});
            skLineSegment(sketch, "E355", {"start": v(-20.35, 128.4) * mm, "end": v(-19.66, 129.95) * mm});
            skLineSegment(sketch, "E356", {"start": v(-19.66, 129.95) * mm, "end": v(-17.45, 120.63) * mm});
            skLineSegment(sketch, "E357", {"start": v(-17.45, 120.63) * mm, "end": v(-15.28, 111.32) * mm});
            skLineSegment(sketch, "E358", {"start": v(-15.28, 111.32) * mm, "end": v(-12.94, 102.1) * mm});
            skLineSegment(sketch, "E359", {"start": v(-12.94, 102.1) * mm, "end": v(-10.18, 93) * mm});
            skLineSegment(sketch, "E360", {"start": v(-10.18, 93) * mm, "end": v(-6.5, 84.17) * mm});
            skLineSegment(sketch, "E361", {"start": v(-6.5, 84.17) * mm, "end": v(-1.67, 76.16) * mm});
            skLineSegment(sketch, "E362", {"start": v(-1.67, 76.16) * mm, "end": v(4.43, 69.04) * mm});
            skLineSegment(sketch, "E363", {"start": v(4.43, 69.04) * mm, "end": v(11.88, 62.87) * mm});
            skLineSegment(sketch, "E364", {"start": v(11.88, 62.87) * mm, "end": v(12.3, 63.92) * mm});
            skLineSegment(sketch, "E365", {"start": v(12.3, 63.92) * mm, "end": v(12.12, 64.74) * mm});
            skLineSegment(sketch, "E366", {"start": v(12.12, 64.74) * mm, "end": v(11.63, 65.41) * mm});
            skLineSegment(sketch, "E367", {"start": v(11.63, 65.41) * mm, "end": v(11.13, 66.03) * mm});
            skLineSegment(sketch, "E368", {"start": v(11.13, 66.03) * mm, "end": v(0.9, 85.65) * mm});
            skLineSegment(sketch, "E369", {"start": v(0.9, 85.65) * mm, "end": v(-4.59, 105.99) * mm});
            skLineSegment(sketch, "E370", {"start": v(-4.59, 105.99) * mm, "end": v(-5.36, 127.02) * mm});
            skLineSegment(sketch, "E371", {"start": v(-5.36, 127.02) * mm, "end": v(-1.4, 148.72) * mm});
            skLineSegment(sketch, "E372", {"start": v(-1.4, 148.72) * mm, "end": v(4.31, 166.31) * mm});
            skLineSegment(sketch, "E373", {"start": v(4.31, 166.31) * mm, "end": v(11.04, 183.52) * mm});
            skLineSegment(sketch, "E374", {"start": v(11.04, 183.52) * mm, "end": v(18.48, 200.45) * mm});
            skLineSegment(sketch, "E375", {"start": v(18.48, 200.45) * mm, "end": v(26.33, 217.2) * mm});
            skLineSegment(sketch, "E376", {"start": v(26.33, 217.2) * mm, "end": v(26.56, 217.62) * mm});
            skLineSegment(sketch, "E377", {"start": v(26.56, 217.62) * mm, "end": v(26.84, 218.01) * mm});
            skLineSegment(sketch, "E378", {"start": v(26.84, 218.01) * mm, "end": v(27.13, 218.4) * mm});
            skLineSegment(sketch, "E379", {"start": v(27.13, 218.4) * mm, "end": v(27.4, 218.8) * mm});
            skLineSegment(sketch, "E380", {"start": v(-78.7, 114.4) * mm, "end": v(-63.86, 105.82) * mm});
            skLineSegment(sketch, "E381", {"start": v(-63.86, 105.82) * mm, "end": v(-54.58, 96.18) * mm});
            skLineSegment(sketch, "E382", {"start": v(-54.58, 96.18) * mm, "end": v(-50.07, 85.05) * mm});
            skLineSegment(sketch, "E383", {"start": v(-50.07, 85.05) * mm, "end": v(-49.49, 71.97) * mm});
            skLineSegment(sketch, "E384", {"start": v(-49.49, 71.97) * mm, "end": v(-50.41, 65.15) * mm});
            skLineSegment(sketch, "E385", {"start": v(-50.41, 65.15) * mm, "end": v(-52.02, 58.5) * mm});
            skLineSegment(sketch, "E386", {"start": v(-52.02, 58.5) * mm, "end": v(-54.19, 51.99) * mm});
            skLineSegment(sketch, "E387", {"start": v(-54.19, 51.99) * mm, "end": v(-56.78, 45.6) * mm});
            skLineSegment(sketch, "E388", {"start": v(-56.78, 45.6) * mm, "end": v(-58.07, 42.77) * mm});
            skLineSegment(sketch, "E389", {"start": v(-58.07, 42.77) * mm, "end": v(-59.42, 39.95) * mm});
            skLineSegment(sketch, "E390", {"start": v(-59.42, 39.95) * mm, "end": v(-60.81, 37.16) * mm});
            skLineSegment(sketch, "E391", {"start": v(-60.81, 37.16) * mm, "end": v(-62.22, 34.37) * mm});
            skLineSegment(sketch, "E392", {"start": v(-62.22, 34.37) * mm, "end": v(-64, 29.42) * mm});
            skLineSegment(sketch, "E393", {"start": v(-64, 29.42) * mm, "end": v(-64.46, 24.45) * mm});
            skLineSegment(sketch, "E394", {"start": v(-64.46, 24.45) * mm, "end": v(-63.86, 19.48) * mm});
            skLineSegment(sketch, "E395", {"start": v(-63.86, 19.48) * mm, "end": v(-62.42, 14.51) * mm});
            skLineSegment(sketch, "E396", {"start": v(-62.42, 14.51) * mm, "end": v(-59.3, 7.28) * mm});
            skLineSegment(sketch, "E397", {"start": v(-59.3, 7.28) * mm, "end": v(-55.44, 0.48) * mm});
            skLineSegment(sketch, "E398", {"start": v(-55.44, 0.48) * mm, "end": v(-47.22, -6.45) * mm});
            skLineSegment(sketch, "E399", {"start": v(-35.1, -21.27) * mm, "end": v(-46.9, -12.85) * mm});
            skLineSegment(sketch, "E400", {"start": v(-46.9, -12.85) * mm, "end": v(-47.21, -13.05) * mm});
            skLineSegment(sketch, "E401", {"start": v(-47.21, -13.05) * mm, "end": v(-47.54, -13.04) * mm});
            skLineSegment(sketch, "E402", {"start": v(-47.54, -13.04) * mm, "end": v(-47.85, -12.88) * mm});
            skLineSegment(sketch, "E403", {"start": v(-47.85, -12.88) * mm, "end": v(-62.64, -0.68) * mm});
            skLineSegment(sketch, "E404", {"start": v(-62.64, -0.68) * mm, "end": v(-75.01, 13.26) * mm});
            skLineSegment(sketch, "E405", {"start": v(-75.01, 13.26) * mm, "end": v(-84.65, 29.18) * mm});
            skLineSegment(sketch, "E406", {"start": v(-84.65, 29.18) * mm, "end": v(-91.25, 47.37) * mm});
            skLineSegment(sketch, "E407", {"start": v(-91.25, 47.37) * mm, "end": v(-91.9, 58.54) * mm});
            skLineSegment(sketch, "E408", {"start": v(-91.9, 58.54) * mm, "end": v(-89.19, 69.99) * mm});
            skLineSegment(sketch, "E409", {"start": v(-89.19, 69.99) * mm, "end": v(-84.17, 79.9) * mm});
            skLineSegment(sketch, "E410", {"start": v(-84.17, 79.9) * mm, "end": v(-77.9, 86.45) * mm});
            skLineSegment(sketch, "E411", {"start": v(-77.9, 86.45) * mm, "end": v(-79.95, 78.62) * mm});
            skLineSegment(sketch, "E412", {"start": v(-79.95, 78.62) * mm, "end": v(-80.36, 70.93) * mm});
            skLineSegment(sketch, "E413", {"start": v(-80.36, 70.93) * mm, "end": v(-78.84, 63.28) * mm});
            skLineSegment(sketch, "E414", {"start": v(-78.84, 63.28) * mm, "end": v(-75.1, 55.55) * mm});
            skLineSegment(sketch, "E415", {"start": v(-75.1, 55.55) * mm, "end": v(-69.64, 70.95) * mm});
            skLineSegment(sketch, "E416", {"start": v(-69.64, 70.95) * mm, "end": v(-66.46, 85.9) * mm});
            skLineSegment(sketch, "E417", {"start": v(-66.46, 85.9) * mm, "end": v(-68.5, 100.4) * mm});
            skLineSegment(sketch, "E418", {"start": v(-68.5, 100.4) * mm, "end": v(-78.7, 114.4) * mm});
            skLineSegment(sketch, "E419", {"start": v(-99.4, -156.08) * mm, "end": v(90.95, -156.08) * mm, "construction": true});
            skSolve(sketch);
        }
        {
            var Q0;
            Q0=makeQuery(id+"F0.imprint","IMPRINT",FACE,{"disambiguationData":[TD([[makeQuery(id+"F0.imprint","IMPRINT",EDGE,{"derivedFrom":sQuery(id+"F0.wireOp",EDGE,"E0")}),-1.0]])]});
            var Q1;
            {var subQ0=sQuery(id+"F0.wireOp",EDGE,"c1845d9d-90f6-424f-85a3-b2f225a6d4a1");Q1=makeQuery(id+"F0.imprint","IMPRINT",FACE,{"disambiguationData":[TD([[makeQuery(id+"F0.imprint","IMPRINT",EDGE,{"derivedFrom":subQ0}),1.0]])]});}
            var Q2;
            Q2=makeQuery(id+"F0.imprint","IMPRINT",FACE,{"disambiguationData":[TD([[makeQuery(id+"F0.imprint","IMPRINT",EDGE,{"derivedFrom":sQuery(id+"F0.wireOp",EDGE,"5d416945-ede6-4732-9b23-e892aec5f9b0")}),1.0]])]});
            extrude(context, id + "F1", {"entities" : qUnion([Q0, Q1, Q2]), "depth" : 8 * mm});
        }
        {
            var Q0;
            Q0=makeQuery(id+"F1.opExtrude","CAP_FACE",FACE,{"disambiguationData":[OSD([sQuery(id+"F0.wireOp",EDGE,"E0"),sQuery(id+"F0.wireOp",EDGE,"E1"),sQuery(id+"F0.wireOp",EDGE,"E2"),sQuery(id+"F0.wireOp",EDGE,"E3"),sQuery(id+"F0.wireOp",EDGE,"E4"),sQuery(id+"F0.wireOp",EDGE,"E5"),sQuery(id+"F0.wireOp",EDGE,"E6"),sQuery(id+"F0.wireOp",EDGE,"E7"),sQuery(id+"F0.wireOp",EDGE,"E8"),sQuery(id+"F0.wireOp",EDGE,"E9"),sQuery(id+"F0.wireOp",EDGE,"E10"),sQuery(id+"F0.wireOp",EDGE,"E11"),sQuery(id+"F0.wireOp",EDGE,"E12"),sQuery(id+"F0.wireOp",EDGE,"E13"),sQuery(id+"F0.wireOp",EDGE,"E14"),sQuery(id+"F0.wireOp",EDGE,"E15"),sQuery(id+"F0.wireOp",EDGE,"E16"),sQuery(id+"F0.wireOp",EDGE,"E17"),sQuery(id+"F0.wireOp",EDGE,"E18"),sQuery(id+"F0.wireOp",EDGE,"E19"),sQuery(id+"F0.wireOp",EDGE,"E20"),sQuery(id+"F0.wireOp",EDGE,"E21"),sQuery(id+"F0.wireOp",EDGE,"E22"),sQuery(id+"F0.wireOp",EDGE,"E23"),sQuery(id+"F0.wireOp",EDGE,"E24"),sQuery(id+"F0.wireOp",EDGE,"E25"),sQuery(id+"F0.wireOp",EDGE,"E26"),sQuery(id+"F0.wireOp",EDGE,"E27"),sQuery(id+"F0.wireOp",EDGE,"E28"),sQuery(id+"F0.wireOp",EDGE,"E29"),sQuery(id+"F0.wireOp",EDGE,"E30"),sQuery(id+"F0.wireOp",EDGE,"E31"),sQuery(id+"F0.wireOp",EDGE,"E32"),sQuery(id+"F0.wireOp",EDGE,"E33"),sQuery(id+"F0.wireOp",EDGE,"E34"),sQuery(id+"F0.wireOp",EDGE,"E35"),sQuery(id+"F0.wireOp",EDGE,"E36"),sQuery(id+"F0.wireOp",EDGE,"E37"),sQuery(id+"F0.wireOp",EDGE,"E38"),sQuery(id+"F0.wireOp",EDGE,"E39"),sQuery(id+"F0.wireOp",EDGE,"E40"),sQuery(id+"F0.wireOp",EDGE,"E41"),sQuery(id+"F0.wireOp",EDGE,"E42"),sQuery(id+"F0.wireOp",EDGE,"E43"),sQuery(id+"F0.wireOp",EDGE,"E44"),sQuery(id+"F0.wireOp",EDGE,"E45"),sQuery(id+"F0.wireOp",EDGE,"E46"),sQuery(id+"F0.wireOp",EDGE,"E47"),sQuery(id+"F0.wireOp",EDGE,"E48"),sQuery(id+"F0.wireOp",EDGE,"E49"),sQuery(id+"F0.wireOp",EDGE,"E50"),sQuery(id+"F0.wireOp",EDGE,"E51"),sQuery(id+"F0.wireOp",EDGE,"E52"),sQuery(id+"F0.wireOp",EDGE,"E53"),sQuery(id+"F0.wireOp",EDGE,"E54"),sQuery(id+"F0.wireOp",EDGE,"E55"),sQuery(id+"F0.wireOp",EDGE,"E56"),sQuery(id+"F0.wireOp",EDGE,"E57"),sQuery(id+"F0.wireOp",EDGE,"E58"),sQuery(id+"F0.wireOp",EDGE,"E59"),sQuery(id+"F0.wireOp",EDGE,"E60"),sQuery(id+"F0.wireOp",EDGE,"E61"),sQuery(id+"F0.wireOp",EDGE,"E62"),sQuery(id+"F0.wireOp",EDGE,"E63"),sQuery(id+"F0.wireOp",EDGE,"E64"),sQuery(id+"F0.wireOp",EDGE,"E65"),sQuery(id+"F0.wireOp",EDGE,"E66"),sQuery(id+"F0.wireOp",EDGE,"E67"),sQuery(id+"F0.wireOp",EDGE,"E68"),sQuery(id+"F0.wireOp",EDGE,"E69"),sQuery(id+"F0.wireOp",EDGE,"E70"),sQuery(id+"F0.wireOp",EDGE,"E71"),sQuery(id+"F0.wireOp",EDGE,"E72"),sQuery(id+"F0.wireOp",EDGE,"E73"),sQuery(id+"F0.wireOp",EDGE,"E74"),sQuery(id+"F0.wireOp",EDGE,"E75"),sQuery(id+"F0.wireOp",EDGE,"E76"),sQuery(id+"F0.wireOp",EDGE,"E77"),sQuery(id+"F0.wireOp",EDGE,"E78"),sQuery(id+"F0.wireOp",EDGE,"E79"),sQuery(id+"F0.wireOp",EDGE,"E80"),sQuery(id+"F0.wireOp",EDGE,"E81"),sQuery(id+"F0.wireOp",EDGE,"E82"),sQuery(id+"F0.wireOp",EDGE,"E83"),sQuery(id+"F0.wireOp",EDGE,"E84"),sQuery(id+"F0.wireOp",EDGE,"E85"),sQuery(id+"F0.wireOp",EDGE,"E86"),sQuery(id+"F0.wireOp",EDGE,"E87"),sQuery(id+"F0.wireOp",EDGE,"E88"),sQuery(id+"F0.wireOp",EDGE,"E89"),sQuery(id+"F0.wireOp",EDGE,"E90"),sQuery(id+"F0.wireOp",EDGE,"E91"),sQuery(id+"F0.wireOp",EDGE,"E92"),sQuery(id+"F0.wireOp",EDGE,"E93"),sQuery(id+"F0.wireOp",EDGE,"E94"),sQuery(id+"F0.wireOp",EDGE,"E95"),sQuery(id+"F0.wireOp",EDGE,"E96"),sQuery(id+"F0.wireOp",EDGE,"E97"),sQuery(id+"F0.wireOp",EDGE,"E98"),sQuery(id+"F0.wireOp",EDGE,"E99"),sQuery(id+"F0.wireOp",EDGE,"E100"),sQuery(id+"F0.wireOp",EDGE,"E101"),sQuery(id+"F0.wireOp",EDGE,"E102"),sQuery(id+"F0.wireOp",EDGE,"E103"),sQuery(id+"F0.wireOp",EDGE,"E104"),sQuery(id+"F0.wireOp",EDGE,"E105"),sQuery(id+"F0.wireOp",EDGE,"E106"),sQuery(id+"F0.wireOp",EDGE,"E107"),sQuery(id+"F0.wireOp",EDGE,"E108"),sQuery(id+"F0.wireOp",EDGE,"E109"),sQuery(id+"F0.wireOp",EDGE,"E110"),sQuery(id+"F0.wireOp",EDGE,"E111"),sQuery(id+"F0.wireOp",EDGE,"E112"),sQuery(id+"F0.wireOp",EDGE,"E113"),sQuery(id+"F0.wireOp",EDGE,"E114"),sQuery(id+"F0.wireOp",EDGE,"E115"),sQuery(id+"F0.wireOp",EDGE,"E116"),sQuery(id+"F0.wireOp",EDGE,"E117"),sQuery(id+"F0.wireOp",EDGE,"E118"),sQuery(id+"F0.wireOp",EDGE,"E119"),sQuery(id+"F0.wireOp",EDGE,"E120"),sQuery(id+"F0.wireOp",EDGE,"E121"),sQuery(id+"F0.wireOp",EDGE,"E122"),sQuery(id+"F0.wireOp",EDGE,"E123"),sQuery(id+"F0.wireOp",EDGE,"E124"),sQuery(id+"F0.wireOp",EDGE,"E125"),sQuery(id+"F0.wireOp",EDGE,"E126"),sQuery(id+"F0.wireOp",EDGE,"E127"),sQuery(id+"F0.wireOp",EDGE,"E128"),sQuery(id+"F0.wireOp",EDGE,"E129"),sQuery(id+"F0.wireOp",EDGE,"E130"),sQuery(id+"F0.wireOp",EDGE,"E131"),sQuery(id+"F0.wireOp",EDGE,"E132"),sQuery(id+"F0.wireOp",EDGE,"E133"),sQuery(id+"F0.wireOp",EDGE,"E134"),sQuery(id+"F0.wireOp",EDGE,"E135"),sQuery(id+"F0.wireOp",EDGE,"E136"),sQuery(id+"F0.wireOp",EDGE,"E137"),sQuery(id+"F0.wireOp",EDGE,"E138"),sQuery(id+"F0.wireOp",EDGE,"E139"),sQuery(id+"F0.wireOp",EDGE,"E140"),sQuery(id+"F0.wireOp",EDGE,"E141"),sQuery(id+"F0.wireOp",EDGE,"E142"),sQuery(id+"F0.wireOp",EDGE,"E143"),sQuery(id+"F0.wireOp",EDGE,"E144"),sQuery(id+"F0.wireOp",EDGE,"E145"),sQuery(id+"F0.wireOp",EDGE,"E146"),sQuery(id+"F0.wireOp",EDGE,"E147"),sQuery(id+"F0.wireOp",EDGE,"E148"),sQuery(id+"F0.wireOp",EDGE,"E149"),sQuery(id+"F0.wireOp",EDGE,"E150"),sQuery(id+"F0.wireOp",EDGE,"E151"),sQuery(id+"F0.wireOp",EDGE,"E152"),sQuery(id+"F0.wireOp",EDGE,"E153"),sQuery(id+"F0.wireOp",EDGE,"E154"),sQuery(id+"F0.wireOp",EDGE,"E155"),sQuery(id+"F0.wireOp",EDGE,"E156"),sQuery(id+"F0.wireOp",EDGE,"E157"),sQuery(id+"F0.wireOp",EDGE,"E158"),sQuery(id+"F0.wireOp",EDGE,"E159"),sQuery(id+"F0.wireOp",EDGE,"E160"),sQuery(id+"F0.wireOp",EDGE,"E161"),sQuery(id+"F0.wireOp",EDGE,"E162"),sQuery(id+"F0.wireOp",EDGE,"E163"),sQuery(id+"F0.wireOp",EDGE,"E164"),sQuery(id+"F0.wireOp",EDGE,"E165"),sQuery(id+"F0.wireOp",EDGE,"E166"),sQuery(id+"F0.wireOp",EDGE,"E167"),sQuery(id+"F0.wireOp",EDGE,"E168"),sQuery(id+"F0.wireOp",EDGE,"E169"),sQuery(id+"F0.wireOp",EDGE,"E170"),sQuery(id+"F0.wireOp",EDGE,"E171"),sQuery(id+"F0.wireOp",EDGE,"E172"),sQuery(id+"F0.wireOp",EDGE,"E173"),sQuery(id+"F0.wireOp",EDGE,"E174"),sQuery(id+"F0.wireOp",EDGE,"E175"),sQuery(id+"F0.wireOp",EDGE,"E176"),sQuery(id+"F0.wireOp",EDGE,"E177"),sQuery(id+"F0.wireOp",EDGE,"E178"),sQuery(id+"F0.wireOp",EDGE,"E179"),sQuery(id+"F0.wireOp",EDGE,"E180"),sQuery(id+"F0.wireOp",EDGE,"E181"),sQuery(id+"F0.wireOp",EDGE,"E182"),sQuery(id+"F0.wireOp",EDGE,"E183"),sQuery(id+"F0.wireOp",EDGE,"E184"),sQuery(id+"F0.wireOp",EDGE,"E185"),sQuery(id+"F0.wireOp",EDGE,"E186"),sQuery(id+"F0.wireOp",EDGE,"E187"),sQuery(id+"F0.wireOp",EDGE,"E188"),sQuery(id+"F0.wireOp",EDGE,"E189"),sQuery(id+"F0.wireOp",EDGE,"E190"),sQuery(id+"F0.wireOp",EDGE,"E191"),sQuery(id+"F0.wireOp",EDGE,"E192"),sQuery(id+"F0.wireOp",EDGE,"E193"),sQuery(id+"F0.wireOp",EDGE,"E194"),sQuery(id+"F0.wireOp",EDGE,"E195"),sQuery(id+"F0.wireOp",EDGE,"E196"),sQuery(id+"F0.wireOp",EDGE,"E197"),sQuery(id+"F0.wireOp",EDGE,"E198"),sQuery(id+"F0.wireOp",EDGE,"E199"),sQuery(id+"F0.wireOp",EDGE,"E200"),sQuery(id+"F0.wireOp",EDGE,"E201"),sQuery(id+"F0.wireOp",EDGE,"E202"),sQuery(id+"F0.wireOp",EDGE,"E203"),sQuery(id+"F0.wireOp",EDGE,"E204"),sQuery(id+"F0.wireOp",EDGE,"E205"),sQuery(id+"F0.wireOp",EDGE,"E206"),sQuery(id+"F0.wireOp",EDGE,"E207"),sQuery(id+"F0.wireOp",EDGE,"E208"),sQuery(id+"F0.wireOp",EDGE,"E209"),sQuery(id+"F0.wireOp",EDGE,"E210"),sQuery(id+"F0.wireOp",EDGE,"E211"),sQuery(id+"F0.wireOp",EDGE,"E212"),sQuery(id+"F0.wireOp",EDGE,"E213"),sQuery(id+"F0.wireOp",EDGE,"E214"),sQuery(id+"F0.wireOp",EDGE,"E215"),sQuery(id+"F0.wireOp",EDGE,"E216"),sQuery(id+"F0.wireOp",EDGE,"E217"),sQuery(id+"F0.wireOp",EDGE,"E218"),sQuery(id+"F0.wireOp",EDGE,"E219"),sQuery(id+"F0.wireOp",EDGE,"E220"),sQuery(id+"F0.wireOp",EDGE,"E221"),sQuery(id+"F0.wireOp",EDGE,"E222"),sQuery(id+"F0.wireOp",EDGE,"E223"),sQuery(id+"F0.wireOp",EDGE,"E224"),sQuery(id+"F0.wireOp",EDGE,"E225"),sQuery(id+"F0.wireOp",EDGE,"E226"),sQuery(id+"F0.wireOp",EDGE,"E227"),sQuery(id+"F0.wireOp",EDGE,"E228"),sQuery(id+"F0.wireOp",EDGE,"E229"),sQuery(id+"F0.wireOp",EDGE,"E230"),sQuery(id+"F0.wireOp",EDGE,"E231"),sQuery(id+"F0.wireOp",EDGE,"E232"),sQuery(id+"F0.wireOp",EDGE,"E233"),sQuery(id+"F0.wireOp",EDGE,"E234"),sQuery(id+"F0.wireOp",EDGE,"E235"),sQuery(id+"F0.wireOp",EDGE,"E236"),sQuery(id+"F0.wireOp",EDGE,"E237"),sQuery(id+"F0.wireOp",EDGE,"E238"),sQuery(id+"F0.wireOp",EDGE,"E239"),sQuery(id+"F0.wireOp",EDGE,"E240"),sQuery(id+"F0.wireOp",EDGE,"E241"),sQuery(id+"F0.wireOp",EDGE,"E242"),sQuery(id+"F0.wireOp",EDGE,"E243"),sQuery(id+"F0.wireOp",EDGE,"E244"),sQuery(id+"F0.wireOp",EDGE,"E245"),sQuery(id+"F0.wireOp",EDGE,"E246"),sQuery(id+"F0.wireOp",EDGE,"E247"),sQuery(id+"F0.wireOp",EDGE,"E248"),sQuery(id+"F0.wireOp",EDGE,"E249"),sQuery(id+"F0.wireOp",EDGE,"E250"),sQuery(id+"F0.wireOp",EDGE,"E251"),sQuery(id+"F0.wireOp",EDGE,"E252"),sQuery(id+"F0.wireOp",EDGE,"E253"),sQuery(id+"F0.wireOp",EDGE,"E254"),sQuery(id+"F0.wireOp",EDGE,"E255"),sQuery(id+"F0.wireOp",EDGE,"E256"),sQuery(id+"F0.wireOp",EDGE,"E257"),sQuery(id+"F0.wireOp",EDGE,"E258"),sQuery(id+"F0.wireOp",EDGE,"E259"),sQuery(id+"F0.wireOp",EDGE,"E260"),sQuery(id+"F0.wireOp",EDGE,"E261"),sQuery(id+"F0.wireOp",EDGE,"E262"),sQuery(id+"F0.wireOp",EDGE,"E263"),sQuery(id+"F0.wireOp",EDGE,"E264"),sQuery(id+"F0.wireOp",EDGE,"E265"),sQuery(id+"F0.wireOp",EDGE,"E266"),sQuery(id+"F0.wireOp",EDGE,"E267"),sQuery(id+"F0.wireOp",EDGE,"E268"),sQuery(id+"F0.wireOp",EDGE,"E269"),sQuery(id+"F0.wireOp",EDGE,"E270"),sQuery(id+"F0.wireOp",EDGE,"E271"),sQuery(id+"F0.wireOp",EDGE,"E272"),sQuery(id+"F0.wireOp",EDGE,"E273"),sQuery(id+"F0.wireOp",EDGE,"E274"),sQuery(id+"F0.wireOp",EDGE,"E275"),sQuery(id+"F0.wireOp",EDGE,"E276"),sQuery(id+"F0.wireOp",EDGE,"E277"),sQuery(id+"F0.wireOp",EDGE,"E278"),sQuery(id+"F0.wireOp",EDGE,"E279"),sQuery(id+"F0.wireOp",EDGE,"E280"),sQuery(id+"F0.wireOp",EDGE,"E281"),sQuery(id+"F0.wireOp",EDGE,"E282"),sQuery(id+"F0.wireOp",EDGE,"E283"),sQuery(id+"F0.wireOp",EDGE,"E284"),sQuery(id+"F0.wireOp",EDGE,"E285"),sQuery(id+"F0.wireOp",EDGE,"E286"),sQuery(id+"F0.wireOp",EDGE,"E287"),sQuery(id+"F0.wireOp",EDGE,"E288"),sQuery(id+"F0.wireOp",EDGE,"E289"),sQuery(id+"F0.wireOp",EDGE,"E290"),sQuery(id+"F0.wireOp",EDGE,"E291"),sQuery(id+"F0.wireOp",EDGE,"E292"),sQuery(id+"F0.wireOp",EDGE,"E293"),sQuery(id+"F0.wireOp",EDGE,"E294"),sQuery(id+"F0.wireOp",EDGE,"E295"),sQuery(id+"F0.wireOp",EDGE,"E296"),sQuery(id+"F0.wireOp",EDGE,"E297"),sQuery(id+"F0.wireOp",EDGE,"E298"),sQuery(id+"F0.wireOp",EDGE,"E299"),sQuery(id+"F0.wireOp",EDGE,"E300"),sQuery(id+"F0.wireOp",EDGE,"E301"),sQuery(id+"F0.wireOp",EDGE,"E302"),sQuery(id+"F0.wireOp",EDGE,"E303"),sQuery(id+"F0.wireOp",EDGE,"E304"),sQuery(id+"F0.wireOp",EDGE,"E305"),sQuery(id+"F0.wireOp",EDGE,"E306"),sQuery(id+"F0.wireOp",EDGE,"E307"),sQuery(id+"F0.wireOp",EDGE,"E308"),sQuery(id+"F0.wireOp",EDGE,"E309"),sQuery(id+"F0.wireOp",EDGE,"E310"),sQuery(id+"F0.wireOp",EDGE,"E311"),sQuery(id+"F0.wireOp",EDGE,"E312"),sQuery(id+"F0.wireOp",EDGE,"E313"),sQuery(id+"F0.wireOp",EDGE,"E314"),sQuery(id+"F0.wireOp",EDGE,"E315"),sQuery(id+"F0.wireOp",EDGE,"E316"),sQuery(id+"F0.wireOp",EDGE,"E317"),sQuery(id+"F0.wireOp",EDGE,"E318"),sQuery(id+"F0.wireOp",EDGE,"E319"),sQuery(id+"F0.wireOp",EDGE,"E320"),sQuery(id+"F0.wireOp",EDGE,"E321"),sQuery(id+"F0.wireOp",EDGE,"E322"),sQuery(id+"F0.wireOp",EDGE,"E323"),sQuery(id+"F0.wireOp",EDGE,"E324"),sQuery(id+"F0.wireOp",EDGE,"E325"),sQuery(id+"F0.wireOp",EDGE,"E326"),sQuery(id+"F0.wireOp",EDGE,"E327"),sQuery(id+"F0.wireOp",EDGE,"E328"),sQuery(id+"F0.wireOp",EDGE,"E329"),sQuery(id+"F0.wireOp",EDGE,"E330"),sQuery(id+"F0.wireOp",EDGE,"E331"),sQuery(id+"F0.wireOp",EDGE,"E332"),sQuery(id+"F0.wireOp",EDGE,"E333"),sQuery(id+"F0.wireOp",EDGE,"E334"),sQuery(id+"F0.wireOp",EDGE,"E335"),sQuery(id+"F0.wireOp",EDGE,"E336"),sQuery(id+"F0.wireOp",EDGE,"E337"),sQuery(id+"F0.wireOp",EDGE,"E338"),sQuery(id+"F0.wireOp",EDGE,"E339"),sQuery(id+"F0.wireOp",EDGE,"E340"),sQuery(id+"F0.wireOp",EDGE,"E341"),sQuery(id+"F0.wireOp",EDGE,"E342"),sQuery(id+"F0.wireOp",EDGE,"E343"),sQuery(id+"F0.wireOp",EDGE,"E344"),sQuery(id+"F0.wireOp",EDGE,"E345"),sQuery(id+"F0.wireOp",EDGE,"E346"),sQuery(id+"F0.wireOp",EDGE,"E347"),sQuery(id+"F0.wireOp",EDGE,"E348"),sQuery(id+"F0.wireOp",EDGE,"E349"),sQuery(id+"F0.wireOp",EDGE,"E350"),sQuery(id+"F0.wireOp",EDGE,"E351"),sQuery(id+"F0.wireOp",EDGE,"E352"),sQuery(id+"F0.wireOp",EDGE,"E353"),sQuery(id+"F0.wireOp",EDGE,"E354"),sQuery(id+"F0.wireOp",EDGE,"E355"),sQuery(id+"F0.wireOp",EDGE,"E356"),sQuery(id+"F0.wireOp",EDGE,"E357"),sQuery(id+"F0.wireOp",EDGE,"E358"),sQuery(id+"F0.wireOp",EDGE,"E359"),sQuery(id+"F0.wireOp",EDGE,"E360"),sQuery(id+"F0.wireOp",EDGE,"E361"),sQuery(id+"F0.wireOp",EDGE,"E362"),sQuery(id+"F0.wireOp",EDGE,"E363"),sQuery(id+"F0.wireOp",EDGE,"E364"),sQuery(id+"F0.wireOp",EDGE,"E365"),sQuery(id+"F0.wireOp",EDGE,"E366"),sQuery(id+"F0.wireOp",EDGE,"E367"),sQuery(id+"F0.wireOp",EDGE,"E368"),sQuery(id+"F0.wireOp",EDGE,"E369"),sQuery(id+"F0.wireOp",EDGE,"E370"),sQuery(id+"F0.wireOp",EDGE,"E371"),sQuery(id+"F0.wireOp",EDGE,"E372"),sQuery(id+"F0.wireOp",EDGE,"E373"),sQuery(id+"F0.wireOp",EDGE,"E374"),sQuery(id+"F0.wireOp",EDGE,"E375"),sQuery(id+"F0.wireOp",EDGE,"E376"),sQuery(id+"F0.wireOp",EDGE,"E377"),sQuery(id+"F0.wireOp",EDGE,"E378"),sQuery(id+"F0.wireOp",EDGE,"E379"),sQuery(id+"F0.wireOp",EDGE,"E380"),sQuery(id+"F0.wireOp",EDGE,"E381"),sQuery(id+"F0.wireOp",EDGE,"E382"),sQuery(id+"F0.wireOp",EDGE,"E383"),sQuery(id+"F0.wireOp",EDGE,"E384"),sQuery(id+"F0.wireOp",EDGE,"E385"),sQuery(id+"F0.wireOp",EDGE,"E386"),sQuery(id+"F0.wireOp",EDGE,"E387"),sQuery(id+"F0.wireOp",EDGE,"E388"),sQuery(id+"F0.wireOp",EDGE,"E389"),sQuery(id+"F0.wireOp",EDGE,"E390"),sQuery(id+"F0.wireOp",EDGE,"E391"),sQuery(id+"F0.wireOp",EDGE,"E392"),sQuery(id+"F0.wireOp",EDGE,"E393"),sQuery(id+"F0.wireOp",EDGE,"E394"),sQuery(id+"F0.wireOp",EDGE,"E395"),sQuery(id+"F0.wireOp",EDGE,"E396"),sQuery(id+"F0.wireOp",EDGE,"E397"),sQuery(id+"F0.wireOp",EDGE,"E398"),sQuery(id+"F0.wireOp",EDGE,"E399"),sQuery(id+"F0.wireOp",EDGE,"E400"),sQuery(id+"F0.wireOp",EDGE,"E401"),sQuery(id+"F0.wireOp",EDGE,"E402"),sQuery(id+"F0.wireOp",EDGE,"E403"),sQuery(id+"F0.wireOp",EDGE,"E404"),sQuery(id+"F0.wireOp",EDGE,"E405"),sQuery(id+"F0.wireOp",EDGE,"E406"),sQuery(id+"F0.wireOp",EDGE,"E407"),sQuery(id+"F0.wireOp",EDGE,"E408"),sQuery(id+"F0.wireOp",EDGE,"E409"),sQuery(id+"F0.wireOp",EDGE,"E410"),sQuery(id+"F0.wireOp",EDGE,"E411"),sQuery(id+"F0.wireOp",EDGE,"E412"),sQuery(id+"F0.wireOp",EDGE,"E413"),sQuery(id+"F0.wireOp",EDGE,"E414"),sQuery(id+"F0.wireOp",EDGE,"E415"),sQuery(id+"F0.wireOp",EDGE,"E416"),sQuery(id+"F0.wireOp",EDGE,"E417"),sQuery(id+"F0.wireOp",EDGE,"E418")])],"isStart":false});
            shell(context, id + "F2", {"entities" : qUnion([Q0]), "thickness" : 4 * mm});
        }
        {
            var Q0;
            Q0=makeQuery(id+"F1.opExtrude","SWEPT_BODY",BODY,{"disambiguationData":[OSD([sQuery(id+"F0.wireOp",EDGE,"E0"),sQuery(id+"F0.wireOp",EDGE,"E1"),sQuery(id+"F0.wireOp",EDGE,"E2"),sQuery(id+"F0.wireOp",EDGE,"E3"),sQuery(id+"F0.wireOp",EDGE,"E4"),sQuery(id+"F0.wireOp",EDGE,"E5"),sQuery(id+"F0.wireOp",EDGE,"E6"),sQuery(id+"F0.wireOp",EDGE,"E7"),sQuery(id+"F0.wireOp",EDGE,"E8"),sQuery(id+"F0.wireOp",EDGE,"E9"),sQuery(id+"F0.wireOp",EDGE,"E10"),sQuery(id+"F0.wireOp",EDGE,"E11"),sQuery(id+"F0.wireOp",EDGE,"E12"),sQuery(id+"F0.wireOp",EDGE,"E13"),sQuery(id+"F0.wireOp",EDGE,"E14"),sQuery(id+"F0.wireOp",EDGE,"E15"),sQuery(id+"F0.wireOp",EDGE,"E16"),sQuery(id+"F0.wireOp",EDGE,"E17"),sQuery(id+"F0.wireOp",EDGE,"E18"),sQuery(id+"F0.wireOp",EDGE,"E19"),sQuery(id+"F0.wireOp",EDGE,"E20"),sQuery(id+"F0.wireOp",EDGE,"E21"),sQuery(id+"F0.wireOp",EDGE,"E22"),sQuery(id+"F0.wireOp",EDGE,"E23"),sQuery(id+"F0.wireOp",EDGE,"E24"),sQuery(id+"F0.wireOp",EDGE,"E25"),sQuery(id+"F0.wireOp",EDGE,"E26"),sQuery(id+"F0.wireOp",EDGE,"E27"),sQuery(id+"F0.wireOp",EDGE,"E28"),sQuery(id+"F0.wireOp",EDGE,"E29"),sQuery(id+"F0.wireOp",EDGE,"E30"),sQuery(id+"F0.wireOp",EDGE,"E31"),sQuery(id+"F0.wireOp",EDGE,"E32"),sQuery(id+"F0.wireOp",EDGE,"E33"),sQuery(id+"F0.wireOp",EDGE,"E34"),sQuery(id+"F0.wireOp",EDGE,"E35"),sQuery(id+"F0.wireOp",EDGE,"E36"),sQuery(id+"F0.wireOp",EDGE,"E37"),sQuery(id+"F0.wireOp",EDGE,"E38"),sQuery(id+"F0.wireOp",EDGE,"E39"),sQuery(id+"F0.wireOp",EDGE,"E40"),sQuery(id+"F0.wireOp",EDGE,"E41"),sQuery(id+"F0.wireOp",EDGE,"E42"),sQuery(id+"F0.wireOp",EDGE,"E43"),sQuery(id+"F0.wireOp",EDGE,"E44"),sQuery(id+"F0.wireOp",EDGE,"E45"),sQuery(id+"F0.wireOp",EDGE,"E46"),sQuery(id+"F0.wireOp",EDGE,"E47"),sQuery(id+"F0.wireOp",EDGE,"E48"),sQuery(id+"F0.wireOp",EDGE,"E49"),sQuery(id+"F0.wireOp",EDGE,"E50"),sQuery(id+"F0.wireOp",EDGE,"E51"),sQuery(id+"F0.wireOp",EDGE,"E52"),sQuery(id+"F0.wireOp",EDGE,"E53"),sQuery(id+"F0.wireOp",EDGE,"E54"),sQuery(id+"F0.wireOp",EDGE,"E55"),sQuery(id+"F0.wireOp",EDGE,"E56"),sQuery(id+"F0.wireOp",EDGE,"E57"),sQuery(id+"F0.wireOp",EDGE,"E58"),sQuery(id+"F0.wireOp",EDGE,"E59"),sQuery(id+"F0.wireOp",EDGE,"E60"),sQuery(id+"F0.wireOp",EDGE,"E61"),sQuery(id+"F0.wireOp",EDGE,"E62"),sQuery(id+"F0.wireOp",EDGE,"E63"),sQuery(id+"F0.wireOp",EDGE,"E64"),sQuery(id+"F0.wireOp",EDGE,"E65"),sQuery(id+"F0.wireOp",EDGE,"E66"),sQuery(id+"F0.wireOp",EDGE,"E67"),sQuery(id+"F0.wireOp",EDGE,"E68"),sQuery(id+"F0.wireOp",EDGE,"E69"),sQuery(id+"F0.wireOp",EDGE,"E70"),sQuery(id+"F0.wireOp",EDGE,"E71"),sQuery(id+"F0.wireOp",EDGE,"E72"),sQuery(id+"F0.wireOp",EDGE,"E73"),sQuery(id+"F0.wireOp",EDGE,"E74"),sQuery(id+"F0.wireOp",EDGE,"E75"),sQuery(id+"F0.wireOp",EDGE,"E76"),sQuery(id+"F0.wireOp",EDGE,"E77"),sQuery(id+"F0.wireOp",EDGE,"E78"),sQuery(id+"F0.wireOp",EDGE,"E79"),sQuery(id+"F0.wireOp",EDGE,"E80"),sQuery(id+"F0.wireOp",EDGE,"E81"),sQuery(id+"F0.wireOp",EDGE,"E82"),sQuery(id+"F0.wireOp",EDGE,"E83"),sQuery(id+"F0.wireOp",EDGE,"E84"),sQuery(id+"F0.wireOp",EDGE,"E85"),sQuery(id+"F0.wireOp",EDGE,"E86"),sQuery(id+"F0.wireOp",EDGE,"E87"),sQuery(id+"F0.wireOp",EDGE,"E88"),sQuery(id+"F0.wireOp",EDGE,"E89"),sQuery(id+"F0.wireOp",EDGE,"E90"),sQuery(id+"F0.wireOp",EDGE,"E91"),sQuery(id+"F0.wireOp",EDGE,"E92"),sQuery(id+"F0.wireOp",EDGE,"E93"),sQuery(id+"F0.wireOp",EDGE,"E94"),sQuery(id+"F0.wireOp",EDGE,"E95"),sQuery(id+"F0.wireOp",EDGE,"E96"),sQuery(id+"F0.wireOp",EDGE,"E97"),sQuery(id+"F0.wireOp",EDGE,"E98"),sQuery(id+"F0.wireOp",EDGE,"E99"),sQuery(id+"F0.wireOp",EDGE,"E100"),sQuery(id+"F0.wireOp",EDGE,"E101"),sQuery(id+"F0.wireOp",EDGE,"E102"),sQuery(id+"F0.wireOp",EDGE,"E103"),sQuery(id+"F0.wireOp",EDGE,"E104"),sQuery(id+"F0.wireOp",EDGE,"E105"),sQuery(id+"F0.wireOp",EDGE,"E106"),sQuery(id+"F0.wireOp",EDGE,"E107"),sQuery(id+"F0.wireOp",EDGE,"E108"),sQuery(id+"F0.wireOp",EDGE,"E109"),sQuery(id+"F0.wireOp",EDGE,"E110"),sQuery(id+"F0.wireOp",EDGE,"E111"),sQuery(id+"F0.wireOp",EDGE,"E112"),sQuery(id+"F0.wireOp",EDGE,"E113"),sQuery(id+"F0.wireOp",EDGE,"E114"),sQuery(id+"F0.wireOp",EDGE,"E115"),sQuery(id+"F0.wireOp",EDGE,"E116"),sQuery(id+"F0.wireOp",EDGE,"E117"),sQuery(id+"F0.wireOp",EDGE,"E118"),sQuery(id+"F0.wireOp",EDGE,"E119"),sQuery(id+"F0.wireOp",EDGE,"E120"),sQuery(id+"F0.wireOp",EDGE,"E121"),sQuery(id+"F0.wireOp",EDGE,"E122"),sQuery(id+"F0.wireOp",EDGE,"E123"),sQuery(id+"F0.wireOp",EDGE,"E124"),sQuery(id+"F0.wireOp",EDGE,"E125"),sQuery(id+"F0.wireOp",EDGE,"E126"),sQuery(id+"F0.wireOp",EDGE,"E127"),sQuery(id+"F0.wireOp",EDGE,"E128"),sQuery(id+"F0.wireOp",EDGE,"E129"),sQuery(id+"F0.wireOp",EDGE,"E130"),sQuery(id+"F0.wireOp",EDGE,"E131"),sQuery(id+"F0.wireOp",EDGE,"E132"),sQuery(id+"F0.wireOp",EDGE,"E133"),sQuery(id+"F0.wireOp",EDGE,"E134"),sQuery(id+"F0.wireOp",EDGE,"E135"),sQuery(id+"F0.wireOp",EDGE,"E136"),sQuery(id+"F0.wireOp",EDGE,"E137"),sQuery(id+"F0.wireOp",EDGE,"E138"),sQuery(id+"F0.wireOp",EDGE,"E139"),sQuery(id+"F0.wireOp",EDGE,"E140"),sQuery(id+"F0.wireOp",EDGE,"E141"),sQuery(id+"F0.wireOp",EDGE,"E142"),sQuery(id+"F0.wireOp",EDGE,"E143"),sQuery(id+"F0.wireOp",EDGE,"E144"),sQuery(id+"F0.wireOp",EDGE,"E145"),sQuery(id+"F0.wireOp",EDGE,"E146"),sQuery(id+"F0.wireOp",EDGE,"E147"),sQuery(id+"F0.wireOp",EDGE,"E148"),sQuery(id+"F0.wireOp",EDGE,"E149"),sQuery(id+"F0.wireOp",EDGE,"E150"),sQuery(id+"F0.wireOp",EDGE,"E151"),sQuery(id+"F0.wireOp",EDGE,"E152"),sQuery(id+"F0.wireOp",EDGE,"E153"),sQuery(id+"F0.wireOp",EDGE,"E154"),sQuery(id+"F0.wireOp",EDGE,"E155"),sQuery(id+"F0.wireOp",EDGE,"E156"),sQuery(id+"F0.wireOp",EDGE,"E157"),sQuery(id+"F0.wireOp",EDGE,"E158"),sQuery(id+"F0.wireOp",EDGE,"E159"),sQuery(id+"F0.wireOp",EDGE,"E160"),sQuery(id+"F0.wireOp",EDGE,"E161"),sQuery(id+"F0.wireOp",EDGE,"E162"),sQuery(id+"F0.wireOp",EDGE,"E163"),sQuery(id+"F0.wireOp",EDGE,"E164"),sQuery(id+"F0.wireOp",EDGE,"E165"),sQuery(id+"F0.wireOp",EDGE,"E166"),sQuery(id+"F0.wireOp",EDGE,"E167"),sQuery(id+"F0.wireOp",EDGE,"E168"),sQuery(id+"F0.wireOp",EDGE,"E169"),sQuery(id+"F0.wireOp",EDGE,"E170"),sQuery(id+"F0.wireOp",EDGE,"E171"),sQuery(id+"F0.wireOp",EDGE,"E172"),sQuery(id+"F0.wireOp",EDGE,"E173"),sQuery(id+"F0.wireOp",EDGE,"E174"),sQuery(id+"F0.wireOp",EDGE,"E175"),sQuery(id+"F0.wireOp",EDGE,"E176"),sQuery(id+"F0.wireOp",EDGE,"E177"),sQuery(id+"F0.wireOp",EDGE,"E178"),sQuery(id+"F0.wireOp",EDGE,"E179"),sQuery(id+"F0.wireOp",EDGE,"E180"),sQuery(id+"F0.wireOp",EDGE,"E181"),sQuery(id+"F0.wireOp",EDGE,"E182"),sQuery(id+"F0.wireOp",EDGE,"E183"),sQuery(id+"F0.wireOp",EDGE,"E184"),sQuery(id+"F0.wireOp",EDGE,"E185"),sQuery(id+"F0.wireOp",EDGE,"E186"),sQuery(id+"F0.wireOp",EDGE,"E187"),sQuery(id+"F0.wireOp",EDGE,"E188"),sQuery(id+"F0.wireOp",EDGE,"E189"),sQuery(id+"F0.wireOp",EDGE,"E190"),sQuery(id+"F0.wireOp",EDGE,"E191"),sQuery(id+"F0.wireOp",EDGE,"E192"),sQuery(id+"F0.wireOp",EDGE,"E193"),sQuery(id+"F0.wireOp",EDGE,"E194"),sQuery(id+"F0.wireOp",EDGE,"E195"),sQuery(id+"F0.wireOp",EDGE,"E196"),sQuery(id+"F0.wireOp",EDGE,"E197"),sQuery(id+"F0.wireOp",EDGE,"E198"),sQuery(id+"F0.wireOp",EDGE,"E199"),sQuery(id+"F0.wireOp",EDGE,"E200"),sQuery(id+"F0.wireOp",EDGE,"E201"),sQuery(id+"F0.wireOp",EDGE,"E202"),sQuery(id+"F0.wireOp",EDGE,"E203"),sQuery(id+"F0.wireOp",EDGE,"E204"),sQuery(id+"F0.wireOp",EDGE,"E205"),sQuery(id+"F0.wireOp",EDGE,"E206"),sQuery(id+"F0.wireOp",EDGE,"E207"),sQuery(id+"F0.wireOp",EDGE,"E208"),sQuery(id+"F0.wireOp",EDGE,"E209"),sQuery(id+"F0.wireOp",EDGE,"E210"),sQuery(id+"F0.wireOp",EDGE,"E211"),sQuery(id+"F0.wireOp",EDGE,"E212"),sQuery(id+"F0.wireOp",EDGE,"E213"),sQuery(id+"F0.wireOp",EDGE,"E214"),sQuery(id+"F0.wireOp",EDGE,"E215"),sQuery(id+"F0.wireOp",EDGE,"E216"),sQuery(id+"F0.wireOp",EDGE,"E217"),sQuery(id+"F0.wireOp",EDGE,"E218"),sQuery(id+"F0.wireOp",EDGE,"E219"),sQuery(id+"F0.wireOp",EDGE,"E220"),sQuery(id+"F0.wireOp",EDGE,"E221"),sQuery(id+"F0.wireOp",EDGE,"E222"),sQuery(id+"F0.wireOp",EDGE,"E223"),sQuery(id+"F0.wireOp",EDGE,"E224"),sQuery(id+"F0.wireOp",EDGE,"E225"),sQuery(id+"F0.wireOp",EDGE,"E226"),sQuery(id+"F0.wireOp",EDGE,"E227"),sQuery(id+"F0.wireOp",EDGE,"E228"),sQuery(id+"F0.wireOp",EDGE,"E229"),sQuery(id+"F0.wireOp",EDGE,"E230"),sQuery(id+"F0.wireOp",EDGE,"E231"),sQuery(id+"F0.wireOp",EDGE,"E232"),sQuery(id+"F0.wireOp",EDGE,"E233"),sQuery(id+"F0.wireOp",EDGE,"E234"),sQuery(id+"F0.wireOp",EDGE,"E235"),sQuery(id+"F0.wireOp",EDGE,"E236"),sQuery(id+"F0.wireOp",EDGE,"E237"),sQuery(id+"F0.wireOp",EDGE,"E238"),sQuery(id+"F0.wireOp",EDGE,"E239"),sQuery(id+"F0.wireOp",EDGE,"E240"),sQuery(id+"F0.wireOp",EDGE,"E241"),sQuery(id+"F0.wireOp",EDGE,"E242"),sQuery(id+"F0.wireOp",EDGE,"E243"),sQuery(id+"F0.wireOp",EDGE,"E244"),sQuery(id+"F0.wireOp",EDGE,"E245"),sQuery(id+"F0.wireOp",EDGE,"E246"),sQuery(id+"F0.wireOp",EDGE,"E247"),sQuery(id+"F0.wireOp",EDGE,"E248"),sQuery(id+"F0.wireOp",EDGE,"E249"),sQuery(id+"F0.wireOp",EDGE,"E250"),sQuery(id+"F0.wireOp",EDGE,"E251"),sQuery(id+"F0.wireOp",EDGE,"E252"),sQuery(id+"F0.wireOp",EDGE,"E253"),sQuery(id+"F0.wireOp",EDGE,"E254"),sQuery(id+"F0.wireOp",EDGE,"E255"),sQuery(id+"F0.wireOp",EDGE,"E256"),sQuery(id+"F0.wireOp",EDGE,"E257"),sQuery(id+"F0.wireOp",EDGE,"E258"),sQuery(id+"F0.wireOp",EDGE,"E259"),sQuery(id+"F0.wireOp",EDGE,"E260"),sQuery(id+"F0.wireOp",EDGE,"E261"),sQuery(id+"F0.wireOp",EDGE,"E262"),sQuery(id+"F0.wireOp",EDGE,"E263"),sQuery(id+"F0.wireOp",EDGE,"E264"),sQuery(id+"F0.wireOp",EDGE,"E265"),sQuery(id+"F0.wireOp",EDGE,"E266"),sQuery(id+"F0.wireOp",EDGE,"E267"),sQuery(id+"F0.wireOp",EDGE,"E268"),sQuery(id+"F0.wireOp",EDGE,"E269"),sQuery(id+"F0.wireOp",EDGE,"E270"),sQuery(id+"F0.wireOp",EDGE,"E271"),sQuery(id+"F0.wireOp",EDGE,"E272"),sQuery(id+"F0.wireOp",EDGE,"E273"),sQuery(id+"F0.wireOp",EDGE,"E274"),sQuery(id+"F0.wireOp",EDGE,"E275"),sQuery(id+"F0.wireOp",EDGE,"E276"),sQuery(id+"F0.wireOp",EDGE,"E277"),sQuery(id+"F0.wireOp",EDGE,"E278"),sQuery(id+"F0.wireOp",EDGE,"E279"),sQuery(id+"F0.wireOp",EDGE,"E280"),sQuery(id+"F0.wireOp",EDGE,"E281"),sQuery(id+"F0.wireOp",EDGE,"E282"),sQuery(id+"F0.wireOp",EDGE,"E283"),sQuery(id+"F0.wireOp",EDGE,"E284"),sQuery(id+"F0.wireOp",EDGE,"E285"),sQuery(id+"F0.wireOp",EDGE,"E286"),sQuery(id+"F0.wireOp",EDGE,"E287"),sQuery(id+"F0.wireOp",EDGE,"E288"),sQuery(id+"F0.wireOp",EDGE,"E289"),sQuery(id+"F0.wireOp",EDGE,"E290"),sQuery(id+"F0.wireOp",EDGE,"E291"),sQuery(id+"F0.wireOp",EDGE,"E292"),sQuery(id+"F0.wireOp",EDGE,"E293"),sQuery(id+"F0.wireOp",EDGE,"E294"),sQuery(id+"F0.wireOp",EDGE,"E295"),sQuery(id+"F0.wireOp",EDGE,"E296"),sQuery(id+"F0.wireOp",EDGE,"E297"),sQuery(id+"F0.wireOp",EDGE,"E298"),sQuery(id+"F0.wireOp",EDGE,"E299"),sQuery(id+"F0.wireOp",EDGE,"E300"),sQuery(id+"F0.wireOp",EDGE,"E301"),sQuery(id+"F0.wireOp",EDGE,"E302"),sQuery(id+"F0.wireOp",EDGE,"E303"),sQuery(id+"F0.wireOp",EDGE,"E304"),sQuery(id+"F0.wireOp",EDGE,"E305"),sQuery(id+"F0.wireOp",EDGE,"E306"),sQuery(id+"F0.wireOp",EDGE,"E307"),sQuery(id+"F0.wireOp",EDGE,"E308"),sQuery(id+"F0.wireOp",EDGE,"E309"),sQuery(id+"F0.wireOp",EDGE,"E310"),sQuery(id+"F0.wireOp",EDGE,"E311"),sQuery(id+"F0.wireOp",EDGE,"E312"),sQuery(id+"F0.wireOp",EDGE,"E313"),sQuery(id+"F0.wireOp",EDGE,"E314"),sQuery(id+"F0.wireOp",EDGE,"E315"),sQuery(id+"F0.wireOp",EDGE,"E316"),sQuery(id+"F0.wireOp",EDGE,"E317"),sQuery(id+"F0.wireOp",EDGE,"E318"),sQuery(id+"F0.wireOp",EDGE,"E319"),sQuery(id+"F0.wireOp",EDGE,"E320"),sQuery(id+"F0.wireOp",EDGE,"E321"),sQuery(id+"F0.wireOp",EDGE,"E322"),sQuery(id+"F0.wireOp",EDGE,"E323"),sQuery(id+"F0.wireOp",EDGE,"E324"),sQuery(id+"F0.wireOp",EDGE,"E325"),sQuery(id+"F0.wireOp",EDGE,"E326"),sQuery(id+"F0.wireOp",EDGE,"E327"),sQuery(id+"F0.wireOp",EDGE,"E328"),sQuery(id+"F0.wireOp",EDGE,"E329"),sQuery(id+"F0.wireOp",EDGE,"E330"),sQuery(id+"F0.wireOp",EDGE,"E331"),sQuery(id+"F0.wireOp",EDGE,"E332"),sQuery(id+"F0.wireOp",EDGE,"E333"),sQuery(id+"F0.wireOp",EDGE,"E334"),sQuery(id+"F0.wireOp",EDGE,"E335"),sQuery(id+"F0.wireOp",EDGE,"E336"),sQuery(id+"F0.wireOp",EDGE,"E337"),sQuery(id+"F0.wireOp",EDGE,"E338"),sQuery(id+"F0.wireOp",EDGE,"E339"),sQuery(id+"F0.wireOp",EDGE,"E340"),sQuery(id+"F0.wireOp",EDGE,"E341"),sQuery(id+"F0.wireOp",EDGE,"E342"),sQuery(id+"F0.wireOp",EDGE,"E343"),sQuery(id+"F0.wireOp",EDGE,"E344"),sQuery(id+"F0.wireOp",EDGE,"E345"),sQuery(id+"F0.wireOp",EDGE,"E346"),sQuery(id+"F0.wireOp",EDGE,"E347"),sQuery(id+"F0.wireOp",EDGE,"E348"),sQuery(id+"F0.wireOp",EDGE,"E349"),sQuery(id+"F0.wireOp",EDGE,"E350"),sQuery(id+"F0.wireOp",EDGE,"E351"),sQuery(id+"F0.wireOp",EDGE,"E352"),sQuery(id+"F0.wireOp",EDGE,"E353"),sQuery(id+"F0.wireOp",EDGE,"E354"),sQuery(id+"F0.wireOp",EDGE,"E355"),sQuery(id+"F0.wireOp",EDGE,"E356"),sQuery(id+"F0.wireOp",EDGE,"E357"),sQuery(id+"F0.wireOp",EDGE,"E358"),sQuery(id+"F0.wireOp",EDGE,"E359"),sQuery(id+"F0.wireOp",EDGE,"E360"),sQuery(id+"F0.wireOp",EDGE,"E361"),sQuery(id+"F0.wireOp",EDGE,"E362"),sQuery(id+"F0.wireOp",EDGE,"E363"),sQuery(id+"F0.wireOp",EDGE,"E364"),sQuery(id+"F0.wireOp",EDGE,"E365"),sQuery(id+"F0.wireOp",EDGE,"E366"),sQuery(id+"F0.wireOp",EDGE,"E367"),sQuery(id+"F0.wireOp",EDGE,"E368"),sQuery(id+"F0.wireOp",EDGE,"E369"),sQuery(id+"F0.wireOp",EDGE,"E370"),sQuery(id+"F0.wireOp",EDGE,"E371"),sQuery(id+"F0.wireOp",EDGE,"E372"),sQuery(id+"F0.wireOp",EDGE,"E373"),sQuery(id+"F0.wireOp",EDGE,"E374"),sQuery(id+"F0.wireOp",EDGE,"E375"),sQuery(id+"F0.wireOp",EDGE,"E376"),sQuery(id+"F0.wireOp",EDGE,"E377"),sQuery(id+"F0.wireOp",EDGE,"E378"),sQuery(id+"F0.wireOp",EDGE,"E379"),sQuery(id+"F0.wireOp",EDGE,"E380"),sQuery(id+"F0.wireOp",EDGE,"E381"),sQuery(id+"F0.wireOp",EDGE,"E382"),sQuery(id+"F0.wireOp",EDGE,"E383"),sQuery(id+"F0.wireOp",EDGE,"E384"),sQuery(id+"F0.wireOp",EDGE,"E385"),sQuery(id+"F0.wireOp",EDGE,"E386"),sQuery(id+"F0.wireOp",EDGE,"E387"),sQuery(id+"F0.wireOp",EDGE,"E388"),sQuery(id+"F0.wireOp",EDGE,"E389"),sQuery(id+"F0.wireOp",EDGE,"E390"),sQuery(id+"F0.wireOp",EDGE,"E391"),sQuery(id+"F0.wireOp",EDGE,"E392"),sQuery(id+"F0.wireOp",EDGE,"E393"),sQuery(id+"F0.wireOp",EDGE,"E394"),sQuery(id+"F0.wireOp",EDGE,"E395"),sQuery(id+"F0.wireOp",EDGE,"E396"),sQuery(id+"F0.wireOp",EDGE,"E397"),sQuery(id+"F0.wireOp",EDGE,"E398"),sQuery(id+"F0.wireOp",EDGE,"E399"),sQuery(id+"F0.wireOp",EDGE,"E400"),sQuery(id+"F0.wireOp",EDGE,"E401"),sQuery(id+"F0.wireOp",EDGE,"E402"),sQuery(id+"F0.wireOp",EDGE,"E403"),sQuery(id+"F0.wireOp",EDGE,"E404"),sQuery(id+"F0.wireOp",EDGE,"E405"),sQuery(id+"F0.wireOp",EDGE,"E406"),sQuery(id+"F0.wireOp",EDGE,"E407"),sQuery(id+"F0.wireOp",EDGE,"E408"),sQuery(id+"F0.wireOp",EDGE,"E409"),sQuery(id+"F0.wireOp",EDGE,"E410"),sQuery(id+"F0.wireOp",EDGE,"E411"),sQuery(id+"F0.wireOp",EDGE,"E412"),sQuery(id+"F0.wireOp",EDGE,"E413"),sQuery(id+"F0.wireOp",EDGE,"E414"),sQuery(id+"F0.wireOp",EDGE,"E415"),sQuery(id+"F0.wireOp",EDGE,"E416"),sQuery(id+"F0.wireOp",EDGE,"E417"),sQuery(id+"F0.wireOp",EDGE,"E418")])]});
            var Q1;
            Q1=makeQuery(id+"F1.opExtrude","CAP_VERTEX",VERTEX,{"disambiguationData":[OSD([sQuery(id+"F0.wireOp",EDGE,"E79"),sQuery(id+"F0.wireOp",EDGE,"E80")])],"isStart":true});
            transform(context, id + "F3", {"entities" : qUnion([Q0]), "transformType" : TransformType.SCALE_UNIFORMLY, "scale" : 0.44, "scalePoint" : qUnion([Q1]), "makeCopy" : false});
        }
        {
            var Q0;
            Q0=makeQuery(id+"F1.opExtrude","CAP_FACE",FACE,{"disambiguationData":[OSD([sQuery(id+"F0.wireOp",EDGE,"E0"),sQuery(id+"F0.wireOp",EDGE,"E1"),sQuery(id+"F0.wireOp",EDGE,"E2"),sQuery(id+"F0.wireOp",EDGE,"E3"),sQuery(id+"F0.wireOp",EDGE,"E4"),sQuery(id+"F0.wireOp",EDGE,"E5"),sQuery(id+"F0.wireOp",EDGE,"E6"),sQuery(id+"F0.wireOp",EDGE,"E7"),sQuery(id+"F0.wireOp",EDGE,"E8"),sQuery(id+"F0.wireOp",EDGE,"E9"),sQuery(id+"F0.wireOp",EDGE,"E10"),sQuery(id+"F0.wireOp",EDGE,"E11"),sQuery(id+"F0.wireOp",EDGE,"E12"),sQuery(id+"F0.wireOp",EDGE,"E13"),sQuery(id+"F0.wireOp",EDGE,"E14"),sQuery(id+"F0.wireOp",EDGE,"E15"),sQuery(id+"F0.wireOp",EDGE,"E16"),sQuery(id+"F0.wireOp",EDGE,"E17"),sQuery(id+"F0.wireOp",EDGE,"E18"),sQuery(id+"F0.wireOp",EDGE,"E19"),sQuery(id+"F0.wireOp",EDGE,"E20"),sQuery(id+"F0.wireOp",EDGE,"E21"),sQuery(id+"F0.wireOp",EDGE,"E22"),sQuery(id+"F0.wireOp",EDGE,"E23"),sQuery(id+"F0.wireOp",EDGE,"E24"),sQuery(id+"F0.wireOp",EDGE,"E25"),sQuery(id+"F0.wireOp",EDGE,"E26"),sQuery(id+"F0.wireOp",EDGE,"E27"),sQuery(id+"F0.wireOp",EDGE,"E28"),sQuery(id+"F0.wireOp",EDGE,"E29"),sQuery(id+"F0.wireOp",EDGE,"E30"),sQuery(id+"F0.wireOp",EDGE,"E31"),sQuery(id+"F0.wireOp",EDGE,"E32"),sQuery(id+"F0.wireOp",EDGE,"E33"),sQuery(id+"F0.wireOp",EDGE,"E34"),sQuery(id+"F0.wireOp",EDGE,"E35"),sQuery(id+"F0.wireOp",EDGE,"E36"),sQuery(id+"F0.wireOp",EDGE,"E37"),sQuery(id+"F0.wireOp",EDGE,"E38"),sQuery(id+"F0.wireOp",EDGE,"E39"),sQuery(id+"F0.wireOp",EDGE,"E40"),sQuery(id+"F0.wireOp",EDGE,"E41"),sQuery(id+"F0.wireOp",EDGE,"E42"),sQuery(id+"F0.wireOp",EDGE,"E43"),sQuery(id+"F0.wireOp",EDGE,"E44"),sQuery(id+"F0.wireOp",EDGE,"E45"),sQuery(id+"F0.wireOp",EDGE,"E46"),sQuery(id+"F0.wireOp",EDGE,"E47"),sQuery(id+"F0.wireOp",EDGE,"E48"),sQuery(id+"F0.wireOp",EDGE,"E49"),sQuery(id+"F0.wireOp",EDGE,"E50"),sQuery(id+"F0.wireOp",EDGE,"E51"),sQuery(id+"F0.wireOp",EDGE,"E52"),sQuery(id+"F0.wireOp",EDGE,"E53"),sQuery(id+"F0.wireOp",EDGE,"E54"),sQuery(id+"F0.wireOp",EDGE,"E55"),sQuery(id+"F0.wireOp",EDGE,"E56"),sQuery(id+"F0.wireOp",EDGE,"E57"),sQuery(id+"F0.wireOp",EDGE,"E58"),sQuery(id+"F0.wireOp",EDGE,"E59"),sQuery(id+"F0.wireOp",EDGE,"E60"),sQuery(id+"F0.wireOp",EDGE,"E61"),sQuery(id+"F0.wireOp",EDGE,"E62"),sQuery(id+"F0.wireOp",EDGE,"E63"),sQuery(id+"F0.wireOp",EDGE,"E64"),sQuery(id+"F0.wireOp",EDGE,"E65"),sQuery(id+"F0.wireOp",EDGE,"E66"),sQuery(id+"F0.wireOp",EDGE,"E67"),sQuery(id+"F0.wireOp",EDGE,"E68"),sQuery(id+"F0.wireOp",EDGE,"E69"),sQuery(id+"F0.wireOp",EDGE,"E70"),sQuery(id+"F0.wireOp",EDGE,"E71"),sQuery(id+"F0.wireOp",EDGE,"E72"),sQuery(id+"F0.wireOp",EDGE,"E73"),sQuery(id+"F0.wireOp",EDGE,"E74"),sQuery(id+"F0.wireOp",EDGE,"E75"),sQuery(id+"F0.wireOp",EDGE,"E76"),sQuery(id+"F0.wireOp",EDGE,"E77"),sQuery(id+"F0.wireOp",EDGE,"E78"),sQuery(id+"F0.wireOp",EDGE,"E79"),sQuery(id+"F0.wireOp",EDGE,"E80"),sQuery(id+"F0.wireOp",EDGE,"E81"),sQuery(id+"F0.wireOp",EDGE,"E82"),sQuery(id+"F0.wireOp",EDGE,"E83"),sQuery(id+"F0.wireOp",EDGE,"E84"),sQuery(id+"F0.wireOp",EDGE,"E85"),sQuery(id+"F0.wireOp",EDGE,"E86"),sQuery(id+"F0.wireOp",EDGE,"E87"),sQuery(id+"F0.wireOp",EDGE,"E88"),sQuery(id+"F0.wireOp",EDGE,"E89"),sQuery(id+"F0.wireOp",EDGE,"E90"),sQuery(id+"F0.wireOp",EDGE,"E91"),sQuery(id+"F0.wireOp",EDGE,"E92"),sQuery(id+"F0.wireOp",EDGE,"E93"),sQuery(id+"F0.wireOp",EDGE,"E94"),sQuery(id+"F0.wireOp",EDGE,"E95"),sQuery(id+"F0.wireOp",EDGE,"E96"),sQuery(id+"F0.wireOp",EDGE,"E97"),sQuery(id+"F0.wireOp",EDGE,"E98"),sQuery(id+"F0.wireOp",EDGE,"E99"),sQuery(id+"F0.wireOp",EDGE,"E100"),sQuery(id+"F0.wireOp",EDGE,"E101"),sQuery(id+"F0.wireOp",EDGE,"E102"),sQuery(id+"F0.wireOp",EDGE,"E103"),sQuery(id+"F0.wireOp",EDGE,"E104"),sQuery(id+"F0.wireOp",EDGE,"E105"),sQuery(id+"F0.wireOp",EDGE,"E106"),sQuery(id+"F0.wireOp",EDGE,"E107"),sQuery(id+"F0.wireOp",EDGE,"E108"),sQuery(id+"F0.wireOp",EDGE,"E109"),sQuery(id+"F0.wireOp",EDGE,"E110"),sQuery(id+"F0.wireOp",EDGE,"E111"),sQuery(id+"F0.wireOp",EDGE,"E112"),sQuery(id+"F0.wireOp",EDGE,"E113"),sQuery(id+"F0.wireOp",EDGE,"E114"),sQuery(id+"F0.wireOp",EDGE,"E115"),sQuery(id+"F0.wireOp",EDGE,"E116"),sQuery(id+"F0.wireOp",EDGE,"E117"),sQuery(id+"F0.wireOp",EDGE,"E118"),sQuery(id+"F0.wireOp",EDGE,"E119"),sQuery(id+"F0.wireOp",EDGE,"E120"),sQuery(id+"F0.wireOp",EDGE,"E121"),sQuery(id+"F0.wireOp",EDGE,"E122"),sQuery(id+"F0.wireOp",EDGE,"E123"),sQuery(id+"F0.wireOp",EDGE,"E124"),sQuery(id+"F0.wireOp",EDGE,"E125"),sQuery(id+"F0.wireOp",EDGE,"E126"),sQuery(id+"F0.wireOp",EDGE,"E127"),sQuery(id+"F0.wireOp",EDGE,"E128"),sQuery(id+"F0.wireOp",EDGE,"E129"),sQuery(id+"F0.wireOp",EDGE,"E130"),sQuery(id+"F0.wireOp",EDGE,"E131"),sQuery(id+"F0.wireOp",EDGE,"E132"),sQuery(id+"F0.wireOp",EDGE,"E133"),sQuery(id+"F0.wireOp",EDGE,"E134"),sQuery(id+"F0.wireOp",EDGE,"E135"),sQuery(id+"F0.wireOp",EDGE,"E136"),sQuery(id+"F0.wireOp",EDGE,"E137"),sQuery(id+"F0.wireOp",EDGE,"E138"),sQuery(id+"F0.wireOp",EDGE,"E139"),sQuery(id+"F0.wireOp",EDGE,"E140"),sQuery(id+"F0.wireOp",EDGE,"E141"),sQuery(id+"F0.wireOp",EDGE,"E142"),sQuery(id+"F0.wireOp",EDGE,"E143"),sQuery(id+"F0.wireOp",EDGE,"E144"),sQuery(id+"F0.wireOp",EDGE,"E145"),sQuery(id+"F0.wireOp",EDGE,"E146"),sQuery(id+"F0.wireOp",EDGE,"E147"),sQuery(id+"F0.wireOp",EDGE,"E148"),sQuery(id+"F0.wireOp",EDGE,"E149"),sQuery(id+"F0.wireOp",EDGE,"E150"),sQuery(id+"F0.wireOp",EDGE,"E151"),sQuery(id+"F0.wireOp",EDGE,"E152"),sQuery(id+"F0.wireOp",EDGE,"E153"),sQuery(id+"F0.wireOp",EDGE,"E154"),sQuery(id+"F0.wireOp",EDGE,"E155"),sQuery(id+"F0.wireOp",EDGE,"E156"),sQuery(id+"F0.wireOp",EDGE,"E157"),sQuery(id+"F0.wireOp",EDGE,"E158"),sQuery(id+"F0.wireOp",EDGE,"E159"),sQuery(id+"F0.wireOp",EDGE,"E160"),sQuery(id+"F0.wireOp",EDGE,"E161"),sQuery(id+"F0.wireOp",EDGE,"E162"),sQuery(id+"F0.wireOp",EDGE,"E163"),sQuery(id+"F0.wireOp",EDGE,"E164"),sQuery(id+"F0.wireOp",EDGE,"E165"),sQuery(id+"F0.wireOp",EDGE,"E166"),sQuery(id+"F0.wireOp",EDGE,"E167"),sQuery(id+"F0.wireOp",EDGE,"E168"),sQuery(id+"F0.wireOp",EDGE,"E169"),sQuery(id+"F0.wireOp",EDGE,"E170"),sQuery(id+"F0.wireOp",EDGE,"E171"),sQuery(id+"F0.wireOp",EDGE,"E172"),sQuery(id+"F0.wireOp",EDGE,"E173"),sQuery(id+"F0.wireOp",EDGE,"E174"),sQuery(id+"F0.wireOp",EDGE,"E175"),sQuery(id+"F0.wireOp",EDGE,"E176"),sQuery(id+"F0.wireOp",EDGE,"E177"),sQuery(id+"F0.wireOp",EDGE,"E178"),sQuery(id+"F0.wireOp",EDGE,"E179"),sQuery(id+"F0.wireOp",EDGE,"E180"),sQuery(id+"F0.wireOp",EDGE,"E181"),sQuery(id+"F0.wireOp",EDGE,"E182"),sQuery(id+"F0.wireOp",EDGE,"E183"),sQuery(id+"F0.wireOp",EDGE,"E184"),sQuery(id+"F0.wireOp",EDGE,"E185"),sQuery(id+"F0.wireOp",EDGE,"E186"),sQuery(id+"F0.wireOp",EDGE,"E187"),sQuery(id+"F0.wireOp",EDGE,"E188"),sQuery(id+"F0.wireOp",EDGE,"E189"),sQuery(id+"F0.wireOp",EDGE,"E190"),sQuery(id+"F0.wireOp",EDGE,"E191"),sQuery(id+"F0.wireOp",EDGE,"E192"),sQuery(id+"F0.wireOp",EDGE,"E193"),sQuery(id+"F0.wireOp",EDGE,"E194"),sQuery(id+"F0.wireOp",EDGE,"E195"),sQuery(id+"F0.wireOp",EDGE,"E196"),sQuery(id+"F0.wireOp",EDGE,"E197"),sQuery(id+"F0.wireOp",EDGE,"E198"),sQuery(id+"F0.wireOp",EDGE,"E199"),sQuery(id+"F0.wireOp",EDGE,"E200"),sQuery(id+"F0.wireOp",EDGE,"E201"),sQuery(id+"F0.wireOp",EDGE,"E202"),sQuery(id+"F0.wireOp",EDGE,"E203"),sQuery(id+"F0.wireOp",EDGE,"E204"),sQuery(id+"F0.wireOp",EDGE,"E205"),sQuery(id+"F0.wireOp",EDGE,"E206"),sQuery(id+"F0.wireOp",EDGE,"E207"),sQuery(id+"F0.wireOp",EDGE,"E208"),sQuery(id+"F0.wireOp",EDGE,"E209"),sQuery(id+"F0.wireOp",EDGE,"E210"),sQuery(id+"F0.wireOp",EDGE,"E211"),sQuery(id+"F0.wireOp",EDGE,"E212"),sQuery(id+"F0.wireOp",EDGE,"E213"),sQuery(id+"F0.wireOp",EDGE,"E214"),sQuery(id+"F0.wireOp",EDGE,"E215"),sQuery(id+"F0.wireOp",EDGE,"E216"),sQuery(id+"F0.wireOp",EDGE,"E217"),sQuery(id+"F0.wireOp",EDGE,"E218"),sQuery(id+"F0.wireOp",EDGE,"E219"),sQuery(id+"F0.wireOp",EDGE,"E220"),sQuery(id+"F0.wireOp",EDGE,"E221"),sQuery(id+"F0.wireOp",EDGE,"E222"),sQuery(id+"F0.wireOp",EDGE,"E223"),sQuery(id+"F0.wireOp",EDGE,"E224"),sQuery(id+"F0.wireOp",EDGE,"E225"),sQuery(id+"F0.wireOp",EDGE,"E226"),sQuery(id+"F0.wireOp",EDGE,"E227"),sQuery(id+"F0.wireOp",EDGE,"E228"),sQuery(id+"F0.wireOp",EDGE,"E229"),sQuery(id+"F0.wireOp",EDGE,"E230"),sQuery(id+"F0.wireOp",EDGE,"E231"),sQuery(id+"F0.wireOp",EDGE,"E232"),sQuery(id+"F0.wireOp",EDGE,"E233"),sQuery(id+"F0.wireOp",EDGE,"E234"),sQuery(id+"F0.wireOp",EDGE,"E235"),sQuery(id+"F0.wireOp",EDGE,"E236"),sQuery(id+"F0.wireOp",EDGE,"E237"),sQuery(id+"F0.wireOp",EDGE,"E238"),sQuery(id+"F0.wireOp",EDGE,"E239"),sQuery(id+"F0.wireOp",EDGE,"E240"),sQuery(id+"F0.wireOp",EDGE,"E241"),sQuery(id+"F0.wireOp",EDGE,"E242"),sQuery(id+"F0.wireOp",EDGE,"E243"),sQuery(id+"F0.wireOp",EDGE,"E244"),sQuery(id+"F0.wireOp",EDGE,"E245"),sQuery(id+"F0.wireOp",EDGE,"E246"),sQuery(id+"F0.wireOp",EDGE,"E247"),sQuery(id+"F0.wireOp",EDGE,"E248"),sQuery(id+"F0.wireOp",EDGE,"E249"),sQuery(id+"F0.wireOp",EDGE,"E250"),sQuery(id+"F0.wireOp",EDGE,"E251"),sQuery(id+"F0.wireOp",EDGE,"E252"),sQuery(id+"F0.wireOp",EDGE,"E253"),sQuery(id+"F0.wireOp",EDGE,"E254"),sQuery(id+"F0.wireOp",EDGE,"E255"),sQuery(id+"F0.wireOp",EDGE,"E256"),sQuery(id+"F0.wireOp",EDGE,"E257"),sQuery(id+"F0.wireOp",EDGE,"E258"),sQuery(id+"F0.wireOp",EDGE,"E259"),sQuery(id+"F0.wireOp",EDGE,"E260"),sQuery(id+"F0.wireOp",EDGE,"E261"),sQuery(id+"F0.wireOp",EDGE,"E262"),sQuery(id+"F0.wireOp",EDGE,"E263"),sQuery(id+"F0.wireOp",EDGE,"E264"),sQuery(id+"F0.wireOp",EDGE,"E265"),sQuery(id+"F0.wireOp",EDGE,"E266"),sQuery(id+"F0.wireOp",EDGE,"E267"),sQuery(id+"F0.wireOp",EDGE,"E268"),sQuery(id+"F0.wireOp",EDGE,"E269"),sQuery(id+"F0.wireOp",EDGE,"E270"),sQuery(id+"F0.wireOp",EDGE,"E271"),sQuery(id+"F0.wireOp",EDGE,"E272"),sQuery(id+"F0.wireOp",EDGE,"E273"),sQuery(id+"F0.wireOp",EDGE,"E274"),sQuery(id+"F0.wireOp",EDGE,"E275"),sQuery(id+"F0.wireOp",EDGE,"E276"),sQuery(id+"F0.wireOp",EDGE,"E277"),sQuery(id+"F0.wireOp",EDGE,"E278"),sQuery(id+"F0.wireOp",EDGE,"E279"),sQuery(id+"F0.wireOp",EDGE,"E280"),sQuery(id+"F0.wireOp",EDGE,"E281"),sQuery(id+"F0.wireOp",EDGE,"E282"),sQuery(id+"F0.wireOp",EDGE,"E283"),sQuery(id+"F0.wireOp",EDGE,"E284"),sQuery(id+"F0.wireOp",EDGE,"E285"),sQuery(id+"F0.wireOp",EDGE,"E286"),sQuery(id+"F0.wireOp",EDGE,"E287"),sQuery(id+"F0.wireOp",EDGE,"E288"),sQuery(id+"F0.wireOp",EDGE,"E289"),sQuery(id+"F0.wireOp",EDGE,"E290"),sQuery(id+"F0.wireOp",EDGE,"E291"),sQuery(id+"F0.wireOp",EDGE,"E292"),sQuery(id+"F0.wireOp",EDGE,"E293"),sQuery(id+"F0.wireOp",EDGE,"E294"),sQuery(id+"F0.wireOp",EDGE,"E295"),sQuery(id+"F0.wireOp",EDGE,"E296"),sQuery(id+"F0.wireOp",EDGE,"E297"),sQuery(id+"F0.wireOp",EDGE,"E298"),sQuery(id+"F0.wireOp",EDGE,"E299"),sQuery(id+"F0.wireOp",EDGE,"E300"),sQuery(id+"F0.wireOp",EDGE,"E301"),sQuery(id+"F0.wireOp",EDGE,"E302"),sQuery(id+"F0.wireOp",EDGE,"E303"),sQuery(id+"F0.wireOp",EDGE,"E304"),sQuery(id+"F0.wireOp",EDGE,"E305"),sQuery(id+"F0.wireOp",EDGE,"E306"),sQuery(id+"F0.wireOp",EDGE,"E307"),sQuery(id+"F0.wireOp",EDGE,"E308"),sQuery(id+"F0.wireOp",EDGE,"E309"),sQuery(id+"F0.wireOp",EDGE,"E310"),sQuery(id+"F0.wireOp",EDGE,"E311"),sQuery(id+"F0.wireOp",EDGE,"E312"),sQuery(id+"F0.wireOp",EDGE,"E313"),sQuery(id+"F0.wireOp",EDGE,"E314"),sQuery(id+"F0.wireOp",EDGE,"E315"),sQuery(id+"F0.wireOp",EDGE,"E316"),sQuery(id+"F0.wireOp",EDGE,"E317"),sQuery(id+"F0.wireOp",EDGE,"E318"),sQuery(id+"F0.wireOp",EDGE,"E319"),sQuery(id+"F0.wireOp",EDGE,"E320"),sQuery(id+"F0.wireOp",EDGE,"E321"),sQuery(id+"F0.wireOp",EDGE,"E322"),sQuery(id+"F0.wireOp",EDGE,"E323"),sQuery(id+"F0.wireOp",EDGE,"E324"),sQuery(id+"F0.wireOp",EDGE,"E325"),sQuery(id+"F0.wireOp",EDGE,"E326"),sQuery(id+"F0.wireOp",EDGE,"E327"),sQuery(id+"F0.wireOp",EDGE,"E328"),sQuery(id+"F0.wireOp",EDGE,"E329"),sQuery(id+"F0.wireOp",EDGE,"E330"),sQuery(id+"F0.wireOp",EDGE,"E331"),sQuery(id+"F0.wireOp",EDGE,"E332"),sQuery(id+"F0.wireOp",EDGE,"E333"),sQuery(id+"F0.wireOp",EDGE,"E334"),sQuery(id+"F0.wireOp",EDGE,"E335"),sQuery(id+"F0.wireOp",EDGE,"E336"),sQuery(id+"F0.wireOp",EDGE,"E337"),sQuery(id+"F0.wireOp",EDGE,"E338"),sQuery(id+"F0.wireOp",EDGE,"E339"),sQuery(id+"F0.wireOp",EDGE,"E340"),sQuery(id+"F0.wireOp",EDGE,"E341"),sQuery(id+"F0.wireOp",EDGE,"E342"),sQuery(id+"F0.wireOp",EDGE,"E343"),sQuery(id+"F0.wireOp",EDGE,"E344"),sQuery(id+"F0.wireOp",EDGE,"E345"),sQuery(id+"F0.wireOp",EDGE,"E346"),sQuery(id+"F0.wireOp",EDGE,"E347"),sQuery(id+"F0.wireOp",EDGE,"E348"),sQuery(id+"F0.wireOp",EDGE,"E349"),sQuery(id+"F0.wireOp",EDGE,"E350"),sQuery(id+"F0.wireOp",EDGE,"E351"),sQuery(id+"F0.wireOp",EDGE,"E352"),sQuery(id+"F0.wireOp",EDGE,"E353"),sQuery(id+"F0.wireOp",EDGE,"E354"),sQuery(id+"F0.wireOp",EDGE,"E355"),sQuery(id+"F0.wireOp",EDGE,"E356"),sQuery(id+"F0.wireOp",EDGE,"E357"),sQuery(id+"F0.wireOp",EDGE,"E358"),sQuery(id+"F0.wireOp",EDGE,"E359"),sQuery(id+"F0.wireOp",EDGE,"E360"),sQuery(id+"F0.wireOp",EDGE,"E361"),sQuery(id+"F0.wireOp",EDGE,"E362"),sQuery(id+"F0.wireOp",EDGE,"E363"),sQuery(id+"F0.wireOp",EDGE,"E364"),sQuery(id+"F0.wireOp",EDGE,"E365"),sQuery(id+"F0.wireOp",EDGE,"E366"),sQuery(id+"F0.wireOp",EDGE,"E367"),sQuery(id+"F0.wireOp",EDGE,"E368"),sQuery(id+"F0.wireOp",EDGE,"E369"),sQuery(id+"F0.wireOp",EDGE,"E370"),sQuery(id+"F0.wireOp",EDGE,"E371"),sQuery(id+"F0.wireOp",EDGE,"E372"),sQuery(id+"F0.wireOp",EDGE,"E373"),sQuery(id+"F0.wireOp",EDGE,"E374"),sQuery(id+"F0.wireOp",EDGE,"E375"),sQuery(id+"F0.wireOp",EDGE,"E376"),sQuery(id+"F0.wireOp",EDGE,"E377"),sQuery(id+"F0.wireOp",EDGE,"E378"),sQuery(id+"F0.wireOp",EDGE,"E379"),sQuery(id+"F0.wireOp",EDGE,"E380"),sQuery(id+"F0.wireOp",EDGE,"E381"),sQuery(id+"F0.wireOp",EDGE,"E382"),sQuery(id+"F0.wireOp",EDGE,"E383"),sQuery(id+"F0.wireOp",EDGE,"E384"),sQuery(id+"F0.wireOp",EDGE,"E385"),sQuery(id+"F0.wireOp",EDGE,"E386"),sQuery(id+"F0.wireOp",EDGE,"E387"),sQuery(id+"F0.wireOp",EDGE,"E388"),sQuery(id+"F0.wireOp",EDGE,"E389"),sQuery(id+"F0.wireOp",EDGE,"E390"),sQuery(id+"F0.wireOp",EDGE,"E391"),sQuery(id+"F0.wireOp",EDGE,"E392"),sQuery(id+"F0.wireOp",EDGE,"E393"),sQuery(id+"F0.wireOp",EDGE,"E394"),sQuery(id+"F0.wireOp",EDGE,"E395"),sQuery(id+"F0.wireOp",EDGE,"E396"),sQuery(id+"F0.wireOp",EDGE,"E397"),sQuery(id+"F0.wireOp",EDGE,"E398"),sQuery(id+"F0.wireOp",EDGE,"E399"),sQuery(id+"F0.wireOp",EDGE,"E400"),sQuery(id+"F0.wireOp",EDGE,"E401"),sQuery(id+"F0.wireOp",EDGE,"E402"),sQuery(id+"F0.wireOp",EDGE,"E403"),sQuery(id+"F0.wireOp",EDGE,"E404"),sQuery(id+"F0.wireOp",EDGE,"E405"),sQuery(id+"F0.wireOp",EDGE,"E406"),sQuery(id+"F0.wireOp",EDGE,"E407"),sQuery(id+"F0.wireOp",EDGE,"E408"),sQuery(id+"F0.wireOp",EDGE,"E409"),sQuery(id+"F0.wireOp",EDGE,"E410"),sQuery(id+"F0.wireOp",EDGE,"E411"),sQuery(id+"F0.wireOp",EDGE,"E412"),sQuery(id+"F0.wireOp",EDGE,"E413"),sQuery(id+"F0.wireOp",EDGE,"E414"),sQuery(id+"F0.wireOp",EDGE,"E415"),sQuery(id+"F0.wireOp",EDGE,"E416"),sQuery(id+"F0.wireOp",EDGE,"E417"),sQuery(id+"F0.wireOp",EDGE,"E418")])],"isStart":false});
            var sketch = newSketch(context, id + "F4", { "sketchPlane" : qUnion([Q0])});
            skText(sketch, "E420", { "text": "Michael", "fontName": "RobotoSlab-Bold.ttf"});
            skText(sketch, "E421", { "text": "Rubin", "fontName": "RobotoSlab-Bold.ttf"});
            const initialGuessF4  = {"E420": [-0.04854, -0.03776, 1, 0, 0.01115], "E421": [-0.06716, -0.06783, 1, 0, 0.0249]};
            skSetInitialGuess(sketch, initialGuessF4);
            skSolve(sketch);
        }
        {
            var Q0;
            Q0 = qSketchRegion(id + "F4", true);
            extrude(context, id + "F5", {"entities" : qUnion([Q0]), "operationType" : NewBodyOperationType.ADD, "endBound" : BoundingType.SYMMETRIC, "depth" : 4 * mm});
        }
    });
